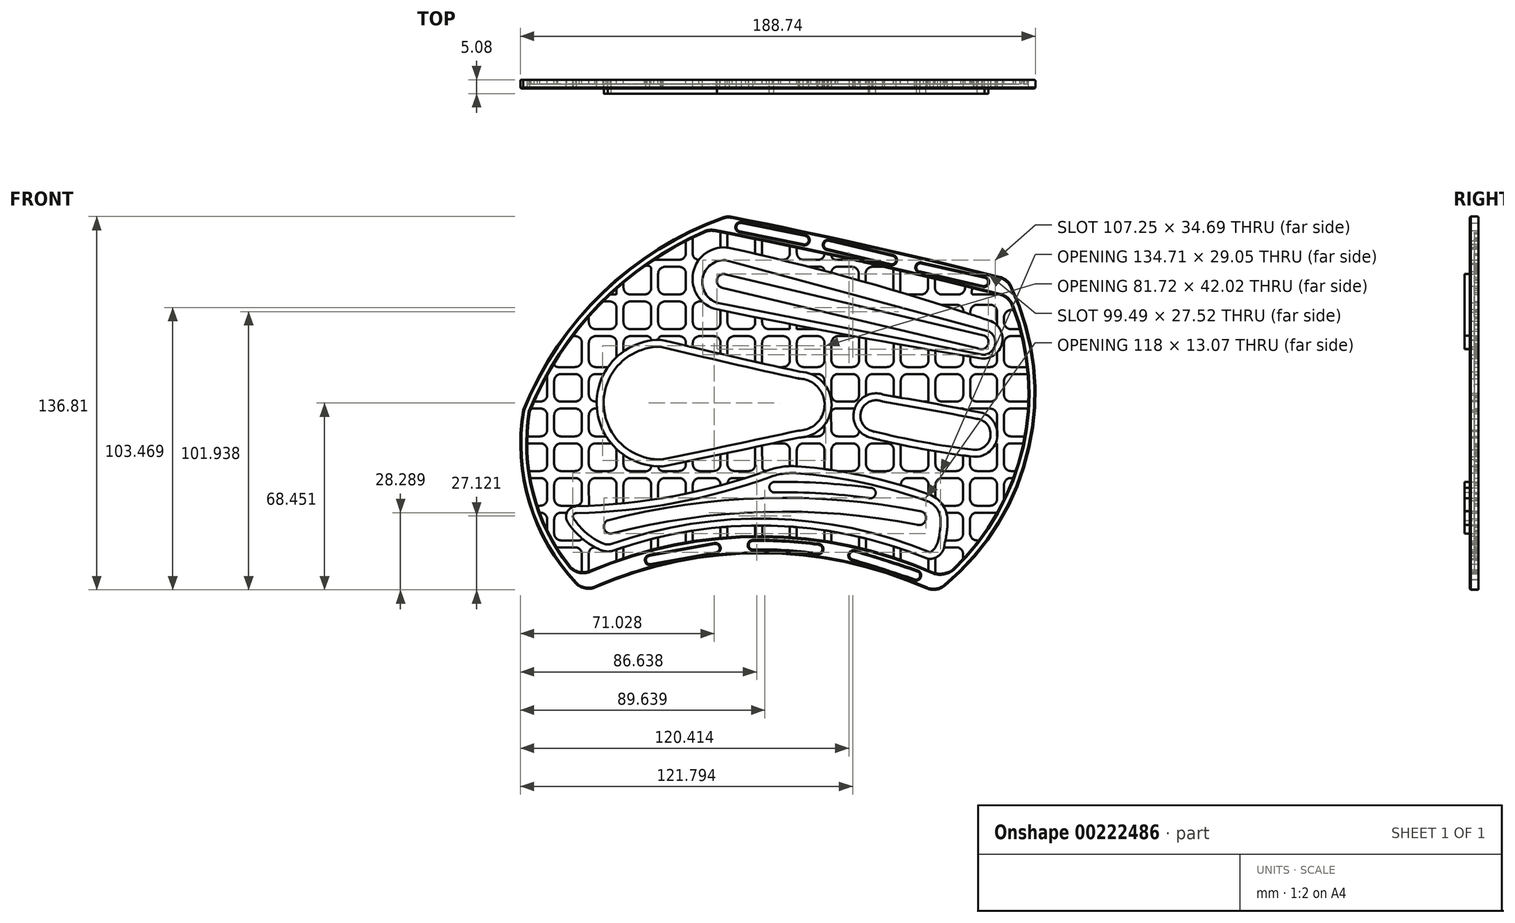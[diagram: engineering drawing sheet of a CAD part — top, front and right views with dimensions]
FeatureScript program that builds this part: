
annotation { "Feature Type Name" : "Feature", "Feature Type Description" : "" }
export const myFeature = defineFeature(function(context is Context, id is Id, definition is map)
    precondition{}
    {
        {
            var Q0;
            Q0=qCreatedBy(makeId("Front.planeOp"),FACE);
            var sketch = newSketch(context, id + "F7", { "sketchPlane" : qUnion([Q0])});
            skPoint(sketch, "E0.middle", {"position": v(0, 0) * mm});
            skPoint(sketch, "E1", {"position": v(94.45, -6.35) * mm});
            skPoint(sketch, "E2", {"position": v(-19.9, 68.07) * mm});
            skPoint(sketch, "E3", {"position": v(-72.19, -69.82) * mm});
            skPoint(sketch, "E4", {"position": v(56.54, -70) * mm});
            skPoint(sketch, "E5", {"position": v(-11.98, -55.6) * mm});
            skPoint(sketch, "E6.0.start.orphan", {"position": v(-11.98, -69.87) * mm});
            skArc(sketch, "E7", {"start": v(53.09, -68.42) * mm, "mid": v(-7.56, -55.54) * mm, "end": v(-68.28, -68.05) * mm});
            skArc(sketch, "E8", {"start": v(80.02, 45.68) * mm, "mid": v(31.06, 57.38) * mm, "end": v(-18.2, 67.74) * mm});
            skArc(sketch, "E9", {"start": v(-21.58, 67.48) * mm, "mid": v(-65.66, 40.06) * mm, "end": v(-94.71, -2.95) * mm});
            skArc(sketch, "E10", {"start": v(-94.71, -2.95) * mm, "mid": v(-92.54, -37.03) * mm, "end": v(-75.43, -66.58) * mm});
            skArc(sketch, "E11", {"start": v(59.69, -67.5) * mm, "mid": v(90.79, -16.84) * mm, "end": v(84.2, 42.24) * mm});
            skArc(sketch, "E12.filletArc", {"start": v(-75.43, -66.58) * mm, "mid": v(-72.08, -68.45) * mm, "end": v(-68.28, -68.05) * mm});
            skArc(sketch, "E13.filletArc", {"start": v(-18.2, 67.74) * mm, "mid": v(-19.9, 67.84) * mm, "end": v(-21.58, 67.48) * mm});
            skPoint(sketch, "E14.visualSharp", {"position": v(82.86, 44.96) * mm});
            skArc(sketch, "E14.filletArc", {"start": v(84.2, 42.24) * mm, "mid": v(82.5, 44.43) * mm, "end": v(80.02, 45.68) * mm});
            skArc(sketch, "E15.filletArc", {"start": v(53.09, -68.42) * mm, "mid": v(56.52, -68.9) * mm, "end": v(59.69, -67.5) * mm});
            skPoint(sketch, "E16.orphan", {"position": v(94.45, 69.85) * mm});
            skPoint(sketch, "E17.orphan", {"position": v(94.45, -69.85) * mm});
            skPoint(sketch, "E0.bottom.end.orphan", {"position": v(-94.45, -69.85) * mm});
            skPoint(sketch, "E0.right.end.orphan", {"position": v(-94.45, 69.85) * mm});
            skArc(sketch, "E18", {"start": v(73.3, 15.83) * mm, "mid": v(80.75, 21.2) * mm, "end": v(76.77, 29.48) * mm});
            skArc(sketch, "E19", {"start": v(-19.12, 56.36) * mm, "mid": v(-32.4, 47.29) * mm, "end": v(-23.6, 33.82) * mm});
            skArc(sketch, "E20", {"start": v(76.77, 29.48) * mm, "mid": v(29.2, 44.24) * mm, "end": v(-19.12, 56.36) * mm});
            skArc(sketch, "E21", {"start": v(-23.6, 33.82) * mm, "mid": v(24.76, 24.32) * mm, "end": v(73.3, 15.83) * mm});
            skArc(sketch, "E22.0", {"start": v(53.4, -57.51) * mm, "mid": v(-3.83, -45.43) * mm, "end": v(-61.62, -54.53) * mm});
            skArc(sketch, "E23", {"start": v(53.4, -57.51) * mm, "mid": v(57.85, -56.25) * mm, "end": v(59.69, -52) * mm});
            skArc(sketch, "E24.0", {"start": v(54.05, -33.95) * mm, "mid": v(30.26, -27.19) * mm, "end": v(5.78, -23.67) * mm});
            skPoint(sketch, "E25.end.orphan", {"position": v(53.09, -41.24) * mm});
            skArc(sketch, "E26", {"start": v(59.69, -52) * mm, "mid": v(60.56, -47.66) * mm, "end": v(60.77, -43.24) * mm});
            skArc(sketch, "E27", {"start": v(-78.33, -44.22) * mm, "mid": v(-73.03, -50.18) * mm, "end": v(-66.24, -54.37) * mm});
            skArc(sketch, "E28", {"start": v(-75.24, -38.32) * mm, "mid": v(-39.47, -34.58) * mm, "end": v(-4.77, -25.12) * mm});
            skPoint(sketch, "E29.visualSharp", {"position": v(0, -23.33) * mm});
            skArc(sketch, "E29.filletArc", {"start": v(5.78, -23.67) * mm, "mid": v(0.43, -23.84) * mm, "end": v(-4.77, -25.12) * mm});
            skPoint(sketch, "E30.visualSharp", {"position": v(-63.76, -55.3) * mm});
            skArc(sketch, "E30.filletArc", {"start": v(-66.24, -54.37) * mm, "mid": v(-63.95, -54.89) * mm, "end": v(-61.62, -54.53) * mm});
            skPoint(sketch, "E31.visualSharp", {"position": v(-81.25, -38.38) * mm});
            skArc(sketch, "E31.filletArc", {"start": v(-75.24, -38.32) * mm, "mid": v(-78.52, -40.36) * mm, "end": v(-78.33, -44.22) * mm});
            skPoint(sketch, "E32.visualSharp", {"position": v(59.69, -36.08) * mm});
            skArc(sketch, "E32.filletArc", {"start": v(60.77, -43.24) * mm, "mid": v(58.85, -37.56) * mm, "end": v(54.05, -33.95) * mm});
            skArc(sketch, "E33", {"start": v(-44.4, 20.12) * mm, "mid": v(-65.2, -0.8) * mm, "end": v(-43.84, -21.14) * mm});
            skArc(sketch, "E34", {"start": v(6.14, -10.59) * mm, "mid": v(15.76, -1.15) * mm, "end": v(6.3, 8.46) * mm});
            skArc(sketch, "E35", {"start": v(-44.4, 20.12) * mm, "mid": v(-19.07, 14.17) * mm, "end": v(6.3, 8.46) * mm});
            skArc(sketch, "E36", {"start": v(-43.84, -21.14) * mm, "mid": v(-18.83, -15.97) * mm, "end": v(6.14, -10.59) * mm});
            skPoint(sketch, "E37.orphan", {"position": v(-94.71, 103.33) * mm});
            skPoint(sketch, "E38.start.orphan", {"position": v(-72.08, -68.45) * mm});
            skArc(sketch, "E39", {"start": v(-20.7, 51.85) * mm, "mid": v(-28.93, 45.34) * mm, "end": v(-23.7, 36.24) * mm});
            skArc(sketch, "E40", {"start": v(73.76, 17.17) * mm, "mid": v(78.2, 20.73) * mm, "end": v(75.72, 25.85) * mm});
            skLineSegment(sketch, "E41", {"start": v(-20.7, 51.85) * mm, "end": v(75.72, 25.85) * mm});
            skLineSegment(sketch, "E42", {"start": v(73.76, 17.17) * mm, "end": v(-23.7, 36.24) * mm});
            skLineSegment(sketch, "E43.0", {"start": v(-21.78, 41.76) * mm, "end": v(71.73, 19.6) * mm});
            skLineSegment(sketch, "E44.0", {"start": v(-20.6, 46.7) * mm, "end": v(74.34, 24.2) * mm});
            skArc(sketch, "E45.0", {"start": v(-43.8, 22.6) * mm, "mid": v(-18.62, 16.67) * mm, "end": v(6.61, 11) * mm});
            skArc(sketch, "E46.0", {"start": v(-44.36, 22.66) * mm, "mid": v(-67.74, -0.82) * mm, "end": v(-43.75, -23.68) * mm});
            skArc(sketch, "E47.0", {"start": v(-43.34, -23.63) * mm, "mid": v(-18.44, -18.48) * mm, "end": v(6.42, -13.13) * mm});
            skArc(sketch, "E48.0", {"start": v(6.42, -13.13) * mm, "mid": v(18.3, -1.16) * mm, "end": v(6.61, 11) * mm});
            skLineSegment(sketch, "E49", {"start": v(-44.36, 22.66) * mm, "end": v(-43.8, 22.6) * mm});
            skLineSegment(sketch, "E50", {"start": v(-43.34, -23.63) * mm, "end": v(-43.75, -23.68) * mm});
            skArc(sketch, "E51.0", {"start": v(55.7, -62.63) * mm, "mid": v(24.98, -52.68) * mm, "end": v(-7.12, -49.2) * mm});
            skArc(sketch, "E52.0", {"start": v(80.08, 39.11) * mm, "mid": v(27.96, 51.57) * mm, "end": v(-24.51, 62.5) * mm});
            skArc(sketch, "E53.0", {"start": v(-28.27, 62.08) * mm, "mid": v(-66.68, 35.46) * mm, "end": v(-92.25, -3.65) * mm});
            skArc(sketch, "E54.0", {"start": v(-92.25, -3.65) * mm, "mid": v(-90.93, -33.4) * mm, "end": v(-77.7, -60.07) * mm});
            skArc(sketch, "E55.0", {"start": v(62.64, -61.51) * mm, "mid": v(88.27, -16.45) * mm, "end": v(84.44, 35.25) * mm});
            skPoint(sketch, "E56.visualSharp", {"position": v(83.19, 38.32) * mm});
            skArc(sketch, "E56.filletArc", {"start": v(84.44, 35.25) * mm, "mid": v(82.73, 37.71) * mm, "end": v(80.08, 39.11) * mm});
            skPoint(sketch, "E57.visualSharp", {"position": v(59.48, -64.36) * mm});
            skPoint(sketch, "E58.visualSharp", {"position": v(-74.47, -63.88) * mm});
            skArc(sketch, "E58.filletArc", {"start": v(-77.7, -60.07) * mm, "mid": v(-74.27, -62.3) * mm, "end": v(-70.2, -61.97) * mm});
            skPoint(sketch, "E59.visualSharp", {"position": v(-26.43, 62.86) * mm});
            skArc(sketch, "E59.filletArc", {"start": v(-24.51, 62.5) * mm, "mid": v(-26.42, 62.57) * mm, "end": v(-28.27, 62.08) * mm});
            skArc(sketch, "E60", {"start": v(37.02, 0) * mm, "mid": v(29.15, -3.47) * mm, "end": v(33.6, -10.83) * mm});
            skArc(sketch, "E61", {"start": v(70.58, -17.65) * mm, "mid": v(76.56, -12.36) * mm, "end": v(71.43, -6.25) * mm});
            skArc(sketch, "E62", {"start": v(71.43, -6.25) * mm, "mid": v(54.25, -2.98) * mm, "end": v(37.02, 0) * mm});
            skArc(sketch, "E63", {"start": v(33.6, -10.83) * mm, "mid": v(51.98, -14.83) * mm, "end": v(70.58, -17.65) * mm});
            skArc(sketch, "E64.0", {"start": v(33.06, -13.31) * mm, "mid": v(51.56, -17.33) * mm, "end": v(70.28, -20.17) * mm});
            skArc(sketch, "E65.0", {"start": v(71.82, -3.74) * mm, "mid": v(54.8, -0.5) * mm, "end": v(37.75, 2.46) * mm});
            skArc(sketch, "E66.0", {"start": v(37.75, 2.46) * mm, "mid": v(26.68, -2.84) * mm, "end": v(33.06, -13.31) * mm});
            skArc(sketch, "E67.0", {"start": v(70.46, -20.18) * mm, "mid": v(79.09, -12.62) * mm, "end": v(71.82, -3.74) * mm});
            skLineSegment(sketch, "E68", {"start": v(70.28, -20.17) * mm, "end": v(70.46, -20.18) * mm});
            skArc(sketch, "E69.0", {"start": v(53, -36.28) * mm, "mid": v(29.6, -29.64) * mm, "end": v(5.5, -26.2) * mm});
            skArc(sketch, "E70.0", {"start": v(54.44, -55.2) * mm, "mid": v(-3.73, -42.9) * mm, "end": v(-62.46, -52.14) * mm});
            skArc(sketch, "E71.0", {"start": v(57.17, -51.58) * mm, "mid": v(58.03, -47.4) * mm, "end": v(58.23, -43.13) * mm});
            skArc(sketch, "E72.0", {"start": v(-75.14, -40.86) * mm, "mid": v(-38.96, -37.06) * mm, "end": v(-3.86, -27.5) * mm});
            skArc(sketch, "E73.0", {"start": v(-76.2, -42.83) * mm, "mid": v(-71.4, -48.24) * mm, "end": v(-65.24, -52.04) * mm});
            skArc(sketch, "E74.0", {"start": v(5.58, -26.2) * mm, "mid": v(0.77, -26.35) * mm, "end": v(-3.9, -27.5) * mm});
            skArc(sketch, "E75", {"start": v(58.23, -43.13) * mm, "mid": v(56.71, -38.87) * mm, "end": v(53, -36.28) * mm});
            skArc(sketch, "E76", {"start": v(54.44, -55.2) * mm, "mid": v(56.15, -53.65) * mm, "end": v(57.17, -51.58) * mm});
            skArc(sketch, "E77", {"start": v(-75.14, -40.86) * mm, "mid": v(-76.33, -41.5) * mm, "end": v(-76.2, -42.83) * mm});
            skArc(sketch, "E78", {"start": v(-65.24, -52.04) * mm, "mid": v(-63.86, -52.32) * mm, "end": v(-62.46, -52.14) * mm});
            skArc(sketch, "E79", {"start": v(50.62, -40.1) * mm, "mid": v(-6.74, -35.32) * mm, "end": v(-63.7, -43.46) * mm});
            skArc(sketch, "E80.0", {"start": v(49.47, -45.04) * mm, "mid": v(-6.66, -40.4) * mm, "end": v(-62.43, -48.37) * mm});
            skArc(sketch, "E81", {"start": v(-63.7, -43.46) * mm, "mid": v(-65.04, -46.43) * mm, "end": v(-62.43, -48.37) * mm});
            skArc(sketch, "E82", {"start": v(31.81, -35.3) * mm, "mid": v(14.54, -33.61) * mm, "end": v(-2.81, -33.24) * mm});
            skArc(sketch, "E83.0", {"start": v(32.32, -31.52) * mm, "mid": v(14.77, -29.8) * mm, "end": v(-2.87, -29.43) * mm});
            skArc(sketch, "E84", {"start": v(-2.87, -29.43) * mm, "mid": v(-4.48, -31.36) * mm, "end": v(-2.81, -33.24) * mm});
            skArc(sketch, "E85", {"start": v(31.81, -35.3) * mm, "mid": v(34.46, -33.73) * mm, "end": v(32.32, -31.52) * mm});
            skArc(sketch, "E86", {"start": v(-20.6, 46.7) * mm, "mid": v(-23.67, 44.82) * mm, "end": v(-21.78, 41.76) * mm});
            skArc(sketch, "E87", {"start": v(71.73, 19.6) * mm, "mid": v(75.46, 20.53) * mm, "end": v(74.34, 24.2) * mm});
            skPoint(sketch, "E88.orphan", {"position": v(73.17, 24.48) * mm});
            skPoint(sketch, "E89.end.orphan", {"position": v(73.17, 19.26) * mm});
            skLineSegment(sketch, "E90.0", {"start": v(-80.78, -50.81) * mm, "end": v(-74, -50.81) * mm});
            skLineSegment(sketch, "E91.0", {"start": v(-89.53, -38.11) * mm, "end": v(-88.4, -38.11) * mm});
            skLineSegment(sketch, "E92.0", {"start": v(-92.51, -25.41) * mm, "end": v(-88.4, -25.41) * mm});
            skLineSegment(sketch, "E93.0", {"start": v(-93.16, -12.71) * mm, "end": v(-88.4, -12.71) * mm});
            skLineSegment(sketch, "E94.0", {"start": v(-62.8, 39.28) * mm, "end": v(-60.46, 39.28) * mm});
            skLineSegment(sketch, "E95.0", {"start": v(-46.77, 51.98) * mm, "end": v(-37.6, 51.98) * mm});
            skLineSegment(sketch, "E96.trimOffspring", {"start": v(-0.33, 51.98) * mm, "end": v(0.5, 51.98) * mm});
            skLineSegment(sketch, "E97.trimOffspring", {"start": v(46.24, 39.28) * mm, "end": v(51.1, 39.28) * mm});
            skLineSegment(sketch, "E98.trimOffspring", {"start": v(84.04, 26.58) * mm, "end": v(87.3, 26.58) * mm});
            skLineSegment(sketch, "E99.trimOffspring", {"start": v(52.03, 0) * mm, "end": v(53.84, 0) * mm});
            skLineSegment(sketch, "E100.trimOffspring", {"start": v(78.96, -12.71) * mm, "end": v(79.08, -12.71) * mm});
            skLineSegment(sketch, "E101.trimOffspring", {"start": v(20.78, 0) * mm, "end": v(25.9, 0) * mm});
            skLineSegment(sketch, "E102.trimOffspring", {"start": v(-82.04, 12.69) * mm, "end": v(-75.7, 12.69) * mm});
            skLineSegment(sketch, "E103.trimOffspring", {"start": v(-1.03, 12.69) * mm, "end": v(0.5, 12.69) * mm});
            skLineSegment(sketch, "E104.trimOffspring", {"start": v(9.38, -12.71) * mm, "end": v(13.16, -12.71) * mm});
            skLineSegment(sketch, "E105.trimOffspring", {"start": v(-90.68, 0.05) * mm, "end": v(-88.4, 0.05) * mm});
            skLineSegment(sketch, "E106.trimOffspring", {"start": v(60, -50.81) * mm, "end": v(63.95, -50.81) * mm});
            skLineSegment(sketch, "E107.trimOffspring", {"start": v(59.22, -38.11) * mm, "end": v(63.95, -38.11) * mm});
            skLineSegment(sketch, "E108.trimOffspring", {"start": v(20.69, -25.41) * mm, "end": v(25.9, -25.41) * mm});
            skArc(sketch, "E109", {"start": v(49.47, -45.04) * mm, "mid": v(52.87, -43.22) * mm, "end": v(50.62, -40.1) * mm});
            skArc(sketch, "E110", {"start": v(55.7, -62.63) * mm, "mid": v(59.31, -62.94) * mm, "end": v(62.64, -61.51) * mm});
            skLineSegment(sketch, "E111.0", {"start": v(56.19, 45.02) * mm, "end": v(56.19, 41.82) * mm});
            skLineSegment(sketch, "E112.0", {"start": v(43.49, 48.02) * mm, "end": v(43.49, 40.1) * mm});
            skLineSegment(sketch, "E113.0", {"start": v(30.79, 46.9) * mm, "end": v(30.79, 43.8) * mm});
            skLineSegment(sketch, "E114.0", {"start": v(-32.52, 60.11) * mm, "end": v(-32.52, 53.86) * mm});
            skLineSegment(sketch, "E115.0", {"start": v(-45.22, 46.9) * mm, "end": v(-45.22, 41.82) * mm});
            skLineSegment(sketch, "E116.0", {"start": v(-57.92, 43.62) * mm, "end": v(-57.92, 41.82) * mm});
            skLineSegment(sketch, "E117.0", {"start": v(-70.62, 31.21) * mm, "end": v(-70.62, 29.12) * mm});
            skLineSegment(sketch, "E118.trimOffspring", {"start": v(69.03, -20.02) * mm, "end": v(69.03, -22.87) * mm});
            skLineSegment(sketch, "E119.trimOffspring", {"start": v(69.1, 16.53) * mm, "end": v(69.1, 15.23) * mm});
            skLineSegment(sketch, "E120.trimOffspring", {"start": v(69.8, 41.7) * mm, "end": v(69.67, 39.82) * mm});
            skLineSegment(sketch, "E121.trimOffspring", {"start": v(43.67, 20.89) * mm, "end": v(43.67, 15.23) * mm});
            skLineSegment(sketch, "E122.trimOffspring", {"start": v(30.97, 23.18) * mm, "end": v(30.97, 15.23) * mm});
            skLineSegment(sketch, "E123.trimOffspring", {"start": v(56.38, 18.67) * mm, "end": v(56.38, 15.23) * mm});
            skLineSegment(sketch, "E124.trimOffspring", {"start": v(18.24, 21.5) * mm, "end": v(18.24, 15.23) * mm});
            skLineSegment(sketch, "E125.trimOffspring", {"start": v(5.58, 56.42) * mm, "end": v(5.58, 54.52) * mm});
            skLineSegment(sketch, "E126.trimOffspring", {"start": v(-7.12, 59.05) * mm, "end": v(-7.12, 53.61) * mm});
            skLineSegment(sketch, "E127.trimOffspring", {"start": v(-19.83, 61.58) * mm, "end": v(-19.83, 56.46) * mm});
            skLineSegment(sketch, "E128.trimOffspring", {"start": v(-70.62, -55.7) * mm, "end": v(-70.62, -62.13) * mm});
            skLineSegment(sketch, "E129.trimOffspring", {"start": v(-57.92, -53.28) * mm, "end": v(-57.92, -57.3) * mm});
            skLineSegment(sketch, "E130.trimOffspring", {"start": v(-45.22, -49.72) * mm, "end": v(-45.22, -53.64) * mm});
            skLineSegment(sketch, "E131.trimOffspring", {"start": v(-32.52, -47.25) * mm, "end": v(-32.52, -51.1) * mm});
            skLineSegment(sketch, "E132.trimOffspring", {"start": v(-19.83, -45.81) * mm, "end": v(-19.83, -49.63) * mm});
            skLineSegment(sketch, "E133.trimOffspring", {"start": v(43.67, -53.87) * mm, "end": v(43.67, -57.9) * mm});
            skLineSegment(sketch, "E134.trimOffspring", {"start": v(56.38, -57.16) * mm, "end": v(56.38, -62.83) * mm});
            skLineSegment(sketch, "E135.trimOffspring", {"start": v(30.97, -50.16) * mm, "end": v(30.97, -54.09) * mm});
            skLineSegment(sketch, "E136.trimOffspring", {"start": v(18.24, -47.53) * mm, "end": v(18.24, -51.4) * mm});
            skLineSegment(sketch, "E137.trimOffspring", {"start": v(5.58, -17.8) * mm, "end": v(5.58, -23.66) * mm});
            skLineSegment(sketch, "E138.trimOffspring", {"start": v(-7.12, -16.07) * mm, "end": v(-7.12, -24.06) * mm});
            skLineSegment(sketch, "E139.trimOffspring", {"start": v(-19.83, -18.78) * mm, "end": v(-19.83, -22.87) * mm});
            skLineSegment(sketch, "E140.trimOffspring", {"start": v(-32.52, -21.42) * mm, "end": v(-32.52, -22.87) * mm});
            skLineSegment(sketch, "E141.trimOffspring", {"start": v(-57.92, -19.46) * mm, "end": v(-57.92, -22.87) * mm});
            skLineSegment(sketch, "E142.trimOffspring", {"start": v(30.97, -12.62) * mm, "end": v(30.97, -12.71) * mm});
            skLineSegment(sketch, "E143.trimOffspring", {"start": v(43.67, -15.77) * mm, "end": v(43.67, -22.87) * mm});
            skLineSegment(sketch, "E144.trimOffspring", {"start": v(56.38, -18.18) * mm, "end": v(56.38, -22.87) * mm});
            skLineSegment(sketch, "E145.0", {"start": v(78.97, 39.4) * mm, "end": v(78.97, 39.28) * mm});
            skLineSegment(sketch, "E146.0", {"start": v(67.3, 42.32) * mm, "end": v(67.25, 41.64) * mm});
            skLineSegment(sketch, "E147.0", {"start": v(53.65, 45.63) * mm, "end": v(53.65, 41.82) * mm});
            skLineSegment(sketch, "E148.trimOffspring", {"start": v(84.04, 33.53) * mm, "end": v(85.09, 33.53) * mm});
            skLineSegment(sketch, "E149.trimOffspring", {"start": v(81.5, 31) * mm, "end": v(81.5, 29.12) * mm});
            skLineSegment(sketch, "E150.trimOffspring", {"start": v(78.96, 33) * mm, "end": v(78.96, 27.94) * mm});
            skLineSegment(sketch, "E151.0", {"start": v(84.04, 24.04) * mm, "end": v(87.95, 24.04) * mm});
            skLineSegment(sketch, "E152.trimOffspring", {"start": v(78.96, 18) * mm, "end": v(78.96, 15.23) * mm});
            skLineSegment(sketch, "E153.trimOffspring", {"start": v(81.5, 21.5) * mm, "end": v(81.5, 15.23) * mm});
            skLineSegment(sketch, "E154.0", {"start": v(10.7, 10.15) * mm, "end": v(13.16, 10.15) * mm});
            skLineSegment(sketch, "E155.trimOffspring", {"start": v(84.04, 12.69) * mm, "end": v(89.93, 12.69) * mm});
            skLineSegment(sketch, "E156.trimOffspring", {"start": v(81.5, 7.6) * mm, "end": v(81.5, 2.54) * mm});
            skLineSegment(sketch, "E157.trimOffspring", {"start": v(84.04, 10.15) * mm, "end": v(90.17, 10.15) * mm});
            skLineSegment(sketch, "E158.trimOffspring", {"start": v(78.96, 7.6) * mm, "end": v(78.96, 2.54) * mm});
            skLineSegment(sketch, "E159.0", {"start": v(65.7, -2.54) * mm, "end": v(66.56, -2.54) * mm});
            skLineSegment(sketch, "E160.trimOffspring", {"start": v(81.5, -5.08) * mm, "end": v(81.5, -10.17) * mm});
            skLineSegment(sketch, "E161.trimOffspring", {"start": v(84.04, 0) * mm, "end": v(90.4, 0) * mm});
            skLineSegment(sketch, "E162.trimOffspring", {"start": v(78.96, -5.08) * mm, "end": v(78.96, -12.71) * mm});
            skLineSegment(sketch, "E163.trimOffspring", {"start": v(84.04, -2.54) * mm, "end": v(90.27, -2.54) * mm});
            skLineSegment(sketch, "E164.0", {"start": v(78.42, -15.25) * mm, "end": v(78.96, -15.25) * mm});
            skLineSegment(sketch, "E165.trimOffspring", {"start": v(84.04, -12.71) * mm, "end": v(89.03, -12.71) * mm});
            skLineSegment(sketch, "E166.trimOffspring", {"start": v(78.96, -15.25) * mm, "end": v(78.96, -22.87) * mm});
            skLineSegment(sketch, "E167.trimOffspring", {"start": v(81.5, -17.8) * mm, "end": v(81.5, -22.87) * mm});
            skLineSegment(sketch, "E168.trimOffspring", {"start": v(84.04, -15.25) * mm, "end": v(88.53, -15.25) * mm});
            skLineSegment(sketch, "E169.trimOffspring", {"start": v(81.5, -30.5) * mm, "end": v(81.5, -35.8) * mm});
            skLineSegment(sketch, "E170.trimOffspring", {"start": v(84.04, -25.41) * mm, "end": v(85.75, -25.41) * mm});
            skLineSegment(sketch, "E171.trimOffspring", {"start": v(84.04, -27.95) * mm, "end": v(84.85, -27.95) * mm});
            skLineSegment(sketch, "E172.trimOffspring", {"start": v(78.96, -30.5) * mm, "end": v(78.96, -35.57) * mm});
            skLineSegment(sketch, "E173.0", {"start": v(66.56, 16.95) * mm, "end": v(66.56, 15.23) * mm});
            skLineSegment(sketch, "E174.0", {"start": v(53.84, 19.11) * mm, "end": v(53.84, 15.23) * mm});
            skLineSegment(sketch, "E175.trimOffspring", {"start": v(69.1, 7.6) * mm, "end": v(69.1, 2.54) * mm});
            skLineSegment(sketch, "E176.trimOffspring", {"start": v(71.64, 12.69) * mm, "end": v(76.42, 12.69) * mm});
            skLineSegment(sketch, "E177.trimOffspring", {"start": v(71.64, 10.15) * mm, "end": v(76.42, 10.15) * mm});
            skLineSegment(sketch, "E178.trimOffspring", {"start": v(66.56, 7.6) * mm, "end": v(66.56, 2.54) * mm});
            skLineSegment(sketch, "E179.trimOffspring", {"start": v(58.92, 0) * mm, "end": v(64.02, 0) * mm});
            skLineSegment(sketch, "E180.trimOffspring", {"start": v(71.64, 0) * mm, "end": v(76.42, 0) * mm});
            skLineSegment(sketch, "E181.trimOffspring", {"start": v(69.1, -2.54) * mm, "end": v(69.1, -3.2) * mm});
            skLineSegment(sketch, "E182.trimOffspring", {"start": v(69.1, -2.54) * mm, "end": v(76.42, -2.54) * mm});
            skLineSegment(sketch, "E183.trimOffspring", {"start": v(66.56, -2.54) * mm, "end": v(66.56, -2.7) * mm});
            skLineSegment(sketch, "E184.trimOffspring", {"start": v(58.92, 12.69) * mm, "end": v(64.02, 12.69) * mm});
            skLineSegment(sketch, "E185.trimOffspring", {"start": v(56.38, 7.6) * mm, "end": v(56.38, 2.54) * mm});
            skLineSegment(sketch, "E186.trimOffspring", {"start": v(58.92, 10.15) * mm, "end": v(64.02, 10.15) * mm});
            skLineSegment(sketch, "E187.trimOffspring", {"start": v(53.84, 7.6) * mm, "end": v(53.84, 0) * mm});
            skLineSegment(sketch, "E188.0", {"start": v(41.13, 21.34) * mm, "end": v(41.13, 15.23) * mm});
            skLineSegment(sketch, "E189.trimOffspring", {"start": v(46.21, 12.69) * mm, "end": v(51.3, 12.69) * mm});
            skLineSegment(sketch, "E190.trimOffspring", {"start": v(43.67, 7.6) * mm, "end": v(43.67, 1.46) * mm});
            skLineSegment(sketch, "E191.trimOffspring", {"start": v(46.21, 10.15) * mm, "end": v(51.3, 10.15) * mm});
            skLineSegment(sketch, "E192.trimOffspring", {"start": v(41.13, 7.6) * mm, "end": v(41.13, 1.9) * mm});
            skLineSegment(sketch, "E193.trimOffspring", {"start": v(58.73, 39.28) * mm, "end": v(64.72, 39.28) * mm});
            skLineSegment(sketch, "E194.trimOffspring", {"start": v(58.35, 35.54) * mm, "end": v(64.1, 35.54) * mm});
            skLineSegment(sketch, "E195.0", {"start": v(40.95, 48.61) * mm, "end": v(40.95, 40.86) * mm});
            skLineSegment(sketch, "E196.0", {"start": v(-85.86, 9.7) * mm, "end": v(-85.86, 2.59) * mm});
            skLineSegment(sketch, "E197.0", {"start": v(-91.78, -2.5) * mm, "end": v(-88.4, -2.5) * mm});
            skLineSegment(sketch, "E198.0", {"start": v(-93.21, -15.25) * mm, "end": v(-88.4, -15.25) * mm});
            skLineSegment(sketch, "E199.0", {"start": v(-92.1, -27.95) * mm, "end": v(-88.4, -27.95) * mm});
            skLineSegment(sketch, "E200.trimOffspring", {"start": v(-80.78, 0.05) * mm, "end": v(-75.7, 0.05) * mm});
            skLineSegment(sketch, "E201.trimOffspring", {"start": v(-83.32, -5.03) * mm, "end": v(-83.32, -10.17) * mm});
            skLineSegment(sketch, "E202.trimOffspring", {"start": v(-80.78, -2.5) * mm, "end": v(-75.7, -2.5) * mm});
            skLineSegment(sketch, "E203.trimOffspring", {"start": v(-85.86, -5.03) * mm, "end": v(-85.86, -10.17) * mm});
            skLineSegment(sketch, "E204.trimOffspring", {"start": v(-80.78, -12.71) * mm, "end": v(-75.7, -12.71) * mm});
            skLineSegment(sketch, "E205.trimOffspring", {"start": v(-80.78, -15.25) * mm, "end": v(-75.7, -15.25) * mm});
            skLineSegment(sketch, "E206.trimOffspring", {"start": v(-83.32, -17.8) * mm, "end": v(-83.32, -22.87) * mm});
            skLineSegment(sketch, "E207.trimOffspring", {"start": v(-85.86, -17.8) * mm, "end": v(-85.86, -22.87) * mm});
            skLineSegment(sketch, "E208.trimOffspring", {"start": v(-80.78, -27.95) * mm, "end": v(-75.7, -27.95) * mm});
            skLineSegment(sketch, "E209.trimOffspring", {"start": v(-80.78, -25.41) * mm, "end": v(-75.7, -25.41) * mm});
            skLineSegment(sketch, "E210.trimOffspring", {"start": v(-83.32, -30.5) * mm, "end": v(-83.32, -35.57) * mm});
            skLineSegment(sketch, "E211.trimOffspring", {"start": v(-85.86, -30.5) * mm, "end": v(-85.86, -35.57) * mm});
            skLineSegment(sketch, "E212.trimOffspring", {"start": v(-68.08, -25.41) * mm, "end": v(-63, -25.41) * mm});
            skLineSegment(sketch, "E213.trimOffspring", {"start": v(-73.16, -30.5) * mm, "end": v(-73.16, -36.22) * mm});
            skLineSegment(sketch, "E214.trimOffspring", {"start": v(-68.08, -12.71) * mm, "end": v(-64.28, -12.71) * mm});
            skLineSegment(sketch, "E215.trimOffspring", {"start": v(-68.08, -15.25) * mm, "end": v(-62.46, -15.25) * mm});
            skLineSegment(sketch, "E216.trimOffspring", {"start": v(-70.62, -17.8) * mm, "end": v(-70.62, -22.87) * mm});
            skLineSegment(sketch, "E217.trimOffspring", {"start": v(-73.16, -17.8) * mm, "end": v(-73.16, -22.87) * mm});
            skLineSegment(sketch, "E218.trimOffspring", {"start": v(-68.08, 0.05) * mm, "end": v(-67.74, 0.05) * mm});
            skLineSegment(sketch, "E219.trimOffspring", {"start": v(-68.08, -2.5) * mm, "end": v(-67.66, -2.5) * mm});
            skLineSegment(sketch, "E220.trimOffspring", {"start": v(-70.62, -5.03) * mm, "end": v(-70.62, -10.17) * mm});
            skLineSegment(sketch, "E221.trimOffspring", {"start": v(-73.16, -5.03) * mm, "end": v(-73.16, -10.17) * mm});
            skLineSegment(sketch, "E222.0", {"start": v(28.43, 23.64) * mm, "end": v(28.43, 15.23) * mm});
            skLineSegment(sketch, "E223.trimOffspring", {"start": v(30.97, 7.6) * mm, "end": v(30.97, 2.23) * mm});
            skLineSegment(sketch, "E224.trimOffspring", {"start": v(28.43, 7.6) * mm, "end": v(28.43, 2.54) * mm});
            skLineSegment(sketch, "E225.trimOffspring", {"start": v(33.51, 12.69) * mm, "end": v(38.6, 12.69) * mm});
            skLineSegment(sketch, "E226.trimOffspring", {"start": v(33.51, 10.15) * mm, "end": v(38.6, 10.15) * mm});
            skLineSegment(sketch, "E227.0", {"start": v(53.84, -17.74) * mm, "end": v(53.84, -22.87) * mm});
            skLineSegment(sketch, "E228.trimOffspring", {"start": v(58.92, -27.95) * mm, "end": v(63.95, -27.95) * mm});
            skLineSegment(sketch, "E229.trimOffspring", {"start": v(58.92, -25.41) * mm, "end": v(63.95, -25.41) * mm});
            skLineSegment(sketch, "E230.trimOffspring", {"start": v(56.38, -30.5) * mm, "end": v(56.38, -35.15) * mm});
            skLineSegment(sketch, "E231.trimOffspring", {"start": v(53.84, -30.5) * mm, "end": v(53.84, -33.88) * mm});
            skLineSegment(sketch, "E232.0", {"start": v(66.5, -19.7) * mm, "end": v(66.5, -22.87) * mm});
            skLineSegment(sketch, "E233.0", {"start": v(60.36, -40.65) * mm, "end": v(63.95, -40.65) * mm});
            skLineSegment(sketch, "E234.trimOffspring", {"start": v(71.57, -25.41) * mm, "end": v(76.42, -25.41) * mm});
            skLineSegment(sketch, "E235.trimOffspring", {"start": v(69.03, -30.5) * mm, "end": v(69.03, -35.57) * mm});
            skLineSegment(sketch, "E236.trimOffspring", {"start": v(71.57, -27.95) * mm, "end": v(76.42, -27.95) * mm});
            skLineSegment(sketch, "E237.trimOffspring", {"start": v(66.5, -30.5) * mm, "end": v(66.5, -35.57) * mm});
            skLineSegment(sketch, "E238.trimOffspring", {"start": v(71.57, -38.11) * mm, "end": v(76.42, -38.11) * mm});
            skLineSegment(sketch, "E239.trimOffspring", {"start": v(66.5, -43.2) * mm, "end": v(66.5, -48.27) * mm});
            skLineSegment(sketch, "E240.trimOffspring", {"start": v(71.57, -40.65) * mm, "end": v(79.2, -40.65) * mm});
            skLineSegment(sketch, "E241.trimOffspring", {"start": v(69.03, -43.2) * mm, "end": v(69.03, -48.27) * mm});
            skLineSegment(sketch, "E242.0", {"start": v(41.13, -17.8) * mm, "end": v(41.13, -22.87) * mm});
            skLineSegment(sketch, "E243.trimOffspring", {"start": v(46.21, -25.41) * mm, "end": v(51.3, -25.41) * mm});
            skLineSegment(sketch, "E244.trimOffspring", {"start": v(46.21, -27.95) * mm, "end": v(51.3, -27.95) * mm});
            skLineSegment(sketch, "E245.trimOffspring", {"start": v(43.67, -30.5) * mm, "end": v(43.67, -30.8) * mm});
            skLineSegment(sketch, "E246.trimOffspring", {"start": v(33.51, -25.41) * mm, "end": v(38.6, -25.41) * mm});
            skLineSegment(sketch, "E247.trimOffspring", {"start": v(70.17, 39.28) * mm, "end": v(78.97, 39.28) * mm});
            skLineSegment(sketch, "E248.trimOffspring", {"start": v(71.73, 35.54) * mm, "end": v(76.42, 35.54) * mm});
            skLineSegment(sketch, "E249.trimOffspring", {"start": v(69.2, 33.18) * mm, "end": v(69.12, 32.05) * mm});
            skLineSegment(sketch, "E250.trimOffspring", {"start": v(66.63, 32.87) * mm, "end": v(66.63, 32.82) * mm});
            skLineSegment(sketch, "E251.0", {"start": v(59.56, -53.35) * mm, "end": v(63.95, -53.35) * mm});
            skLineSegment(sketch, "E252.trimOffspring", {"start": v(71.57, -50.81) * mm, "end": v(72.25, -50.81) * mm});
            skLineSegment(sketch, "E253.trimOffspring", {"start": v(66.5, -55.9) * mm, "end": v(66.5, -57.64) * mm});
            skLineSegment(sketch, "E254", {"start": v(30.97, -17.8) * mm, "end": v(30.97, -22.87) * mm});
            skLineSegment(sketch, "E255.0", {"start": v(28.25, 46.9) * mm, "end": v(28.25, 44.5) * mm});
            skLineSegment(sketch, "E256.0", {"start": v(9.82, 49.44) * mm, "end": v(14.26, 49.44) * mm});
            skLineSegment(sketch, "E257.trimOffspring", {"start": v(33.33, 49.44) * mm, "end": v(37.35, 49.44) * mm});
            skLineSegment(sketch, "E258.trimOffspring", {"start": v(20.42, 49.44) * mm, "end": v(25.7, 49.44) * mm});
            skLineSegment(sketch, "E259.trimOffspring", {"start": v(19.87, 51.98) * mm, "end": v(26.1, 51.98) * mm});
            skLineSegment(sketch, "E260.0", {"start": v(15.7, 21.5) * mm, "end": v(15.7, 15.23) * mm});
            skLineSegment(sketch, "E261.trimOffspring", {"start": v(20.78, 12.69) * mm, "end": v(25.9, 12.69) * mm});
            skLineSegment(sketch, "E262.trimOffspring", {"start": v(20.78, 10.15) * mm, "end": v(25.9, 10.15) * mm});
            skLineSegment(sketch, "E263.trimOffspring", {"start": v(18.24, 7.6) * mm, "end": v(18.24, 2.53) * mm});
            skLineSegment(sketch, "E264.trimOffspring", {"start": v(15.7, 7.6) * mm, "end": v(15.7, 6.42) * mm});
            skLineSegment(sketch, "E265.0", {"start": v(3.04, 56.96) * mm, "end": v(3.04, 54.52) * mm});
            skLineSegment(sketch, "E266.0", {"start": v(-76.5, 24.04) * mm, "end": v(-75.7, 24.04) * mm});
            skLineSegment(sketch, "E267.trimOffspring", {"start": v(5.58, 26.58) * mm, "end": v(12.75, 26.58) * mm});
            skLineSegment(sketch, "E268.trimOffspring", {"start": v(8.12, 24.04) * mm, "end": v(13.16, 24.04) * mm});
            skLineSegment(sketch, "E269.trimOffspring", {"start": v(5.58, 21.5) * mm, "end": v(5.58, 15.23) * mm});
            skLineSegment(sketch, "E270.trimOffspring", {"start": v(3.04, 21.5) * mm, "end": v(3.04, 15.23) * mm});
            skLineSegment(sketch, "E271.trimOffspring", {"start": v(20.78, 24.04) * mm, "end": v(26.27, 24.04) * mm});
            skLineSegment(sketch, "E272.0", {"start": v(-9.66, 59.56) * mm, "end": v(-9.66, 54.2) * mm});
            skLineSegment(sketch, "E273.trimOffspring", {"start": v(-4.58, 24.04) * mm, "end": v(0.5, 24.04) * mm});
            skLineSegment(sketch, "E274.trimOffspring", {"start": v(-4.58, 26.58) * mm, "end": v(3.04, 26.58) * mm});
            skLineSegment(sketch, "E275.trimOffspring", {"start": v(-7.12, 21.5) * mm, "end": v(-7.12, 14.05) * mm});
            skLineSegment(sketch, "E276.trimOffspring", {"start": v(-9.66, 21.5) * mm, "end": v(-9.66, 14.63) * mm});
            skLineSegment(sketch, "E277.trimOffspring", {"start": v(8.12, 12.69) * mm, "end": v(13.16, 12.69) * mm});
            skLineSegment(sketch, "E278.0", {"start": v(19.6, -2.55) * mm, "end": v(26.78, -2.54) * mm});
            skLineSegment(sketch, "E279.trimOffspring", {"start": v(15.7, -8.55) * mm, "end": v(15.7, -10.17) * mm});
            skLineSegment(sketch, "E280.0", {"start": v(-3.31, -15.25) * mm, "end": v(0.5, -15.25) * mm});
            skLineSegment(sketch, "E281.trimOffspring", {"start": v(30.97, -12.71) * mm, "end": v(31.17, -12.71) * mm});
            skLineSegment(sketch, "E282.trimOffspring", {"start": v(33.51, -15.25) * mm, "end": v(38.6, -15.25) * mm});
            skLineSegment(sketch, "E283.trimOffspring", {"start": v(28.43, -17.8) * mm, "end": v(28.43, -22.87) * mm});
            skLineSegment(sketch, "E284.trimOffspring", {"start": v(18.24, -17.8) * mm, "end": v(18.24, -25.04) * mm});
            skLineSegment(sketch, "E285.trimOffspring", {"start": v(20.73, -12.71) * mm, "end": v(26.7, -12.71) * mm});
            skLineSegment(sketch, "E286.trimOffspring", {"start": v(20.78, -15.25) * mm, "end": v(25.9, -15.25) * mm});
            skLineSegment(sketch, "E287.trimOffspring", {"start": v(15.7, -17.8) * mm, "end": v(15.7, -25.04) * mm});
            skLineSegment(sketch, "E288.0", {"start": v(3.04, -17.8) * mm, "end": v(3.04, -23.62) * mm});
            skLineSegment(sketch, "E289.trimOffspring", {"start": v(8.12, -15.25) * mm, "end": v(13.16, -15.25) * mm});
            skLineSegment(sketch, "E290.trimOffspring", {"start": v(5.58, -45.95) * mm, "end": v(5.58, -49.78) * mm});
            skLineSegment(sketch, "E291.trimOffspring", {"start": v(3.04, -45.76) * mm, "end": v(3.04, -49.78) * mm});
            skLineSegment(sketch, "E292.trimOffspring", {"start": v(-7.12, -45.38) * mm, "end": v(-7.12, -49.2) * mm});
            skLineSegment(sketch, "E293.0", {"start": v(-65.42, 36.74) * mm, "end": v(-63, 36.74) * mm});
            skLineSegment(sketch, "E294.0", {"start": v(-22.37, 62.08) * mm, "end": v(-22.37, 56.47) * mm});
            skLineSegment(sketch, "E295.0", {"start": v(-35.06, 58.84) * mm, "end": v(-35.06, 54.52) * mm});
            skLineSegment(sketch, "E296.0", {"start": v(-47.76, 48.9) * mm, "end": v(-47.76, 41.82) * mm});
            skLineSegment(sketch, "E297.0", {"start": v(-60.46, 41.41) * mm, "end": v(-60.46, 39.28) * mm});
            skLineSegment(sketch, "E298.trimOffspring", {"start": v(-17.29, 24.04) * mm, "end": v(-12.2, 24.04) * mm});
            skLineSegment(sketch, "E299.trimOffspring", {"start": v(-17.29, 26.58) * mm, "end": v(-12.2, 26.58) * mm});
            skLineSegment(sketch, "E300.trimOffspring", {"start": v(-22.37, 21.5) * mm, "end": v(-22.37, 17.54) * mm});
            skLineSegment(sketch, "E301.trimOffspring", {"start": v(-19.83, 21.5) * mm, "end": v(-19.83, 16.95) * mm});
            skLineSegment(sketch, "E302.trimOffspring", {"start": v(-29.98, 26.58) * mm, "end": v(-24.9, 26.58) * mm});
            skLineSegment(sketch, "E303.trimOffspring", {"start": v(-29.98, 24.04) * mm, "end": v(-24.9, 24.04) * mm});
            skLineSegment(sketch, "E304.trimOffspring", {"start": v(-35.06, 21.5) * mm, "end": v(-35.06, 20.5) * mm});
            skLineSegment(sketch, "E305.trimOffspring", {"start": v(-32.52, 21.5) * mm, "end": v(-32.52, 19.9) * mm});
            skLineSegment(sketch, "E306.trimOffspring", {"start": v(-32.52, 34.2) * mm, "end": v(-32.52, 29.12) * mm});
            skLineSegment(sketch, "E307.trimOffspring", {"start": v(-35.06, 34.2) * mm, "end": v(-35.06, 29.12) * mm});
            skLineSegment(sketch, "E308.trimOffspring", {"start": v(-29.98, 36.74) * mm, "end": v(-29.08, 36.74) * mm});
            skLineSegment(sketch, "E309.trimOffspring", {"start": v(-45.22, 34.2) * mm, "end": v(-45.22, 29.12) * mm});
            skLineSegment(sketch, "E310.trimOffspring", {"start": v(-42.68, 39.28) * mm, "end": v(-37.6, 39.28) * mm});
            skLineSegment(sketch, "E311.trimOffspring", {"start": v(-42.68, 36.74) * mm, "end": v(-37.6, 36.74) * mm});
            skLineSegment(sketch, "E312.trimOffspring", {"start": v(-42.68, 26.58) * mm, "end": v(-37.6, 26.58) * mm});
            skLineSegment(sketch, "E313.trimOffspring", {"start": v(-44, 24.04) * mm, "end": v(-37.6, 24.04) * mm});
            skLineSegment(sketch, "E314.trimOffspring", {"start": v(-47.76, 34.2) * mm, "end": v(-47.76, 29.12) * mm});
            skLineSegment(sketch, "E315.trimOffspring", {"start": v(-55.38, 39.28) * mm, "end": v(-50.3, 39.28) * mm});
            skLineSegment(sketch, "E316.trimOffspring", {"start": v(-57.92, 34.2) * mm, "end": v(-57.92, 29.12) * mm});
            skLineSegment(sketch, "E317.trimOffspring", {"start": v(-60.46, 34.2) * mm, "end": v(-60.46, 29.12) * mm});
            skLineSegment(sketch, "E318.trimOffspring", {"start": v(-55.38, 36.74) * mm, "end": v(-50.3, 36.74) * mm});
            skLineSegment(sketch, "E319.0", {"start": v(-42.68, 49.44) * mm, "end": v(-37.6, 49.44) * mm});
            skLineSegment(sketch, "E320.trimOffspring", {"start": v(-35.06, 46.9) * mm, "end": v(-35.06, 41.82) * mm});
            skLineSegment(sketch, "E321.trimOffspring", {"start": v(-68.08, 26.58) * mm, "end": v(-63, 26.58) * mm});
            skLineSegment(sketch, "E322.trimOffspring", {"start": v(-73.16, 21.5) * mm, "end": v(-73.16, 15.23) * mm});
            skLineSegment(sketch, "E323.trimOffspring", {"start": v(-70.62, 21.5) * mm, "end": v(-70.62, 15.23) * mm});
            skLineSegment(sketch, "E324.trimOffspring", {"start": v(-68.08, 24.04) * mm, "end": v(-63, 24.04) * mm});
            skLineSegment(sketch, "E325.0", {"start": v(-80.78, 10.15) * mm, "end": v(-75.7, 10.15) * mm});
            skLineSegment(sketch, "E326.trimOffspring", {"start": v(-83.32, 7.6) * mm, "end": v(-83.32, 2.59) * mm});
            skLineSegment(sketch, "E327.trimOffspring", {"start": v(-68.08, 12.69) * mm, "end": v(-63.62, 12.69) * mm});
            skLineSegment(sketch, "E328.trimOffspring", {"start": v(-68.08, 10.15) * mm, "end": v(-65.15, 10.15) * mm});
            skLineSegment(sketch, "E329.trimOffspring", {"start": v(-70.62, 7.6) * mm, "end": v(-70.62, 2.59) * mm});
            skLineSegment(sketch, "E330.trimOffspring", {"start": v(-73.16, 7.6) * mm, "end": v(-73.16, 2.59) * mm});
            skLineSegment(sketch, "E331.trimOffspring", {"start": v(-19.83, 33.04) * mm, "end": v(-19.83, 29.12) * mm});
            skLineSegment(sketch, "E332.trimOffspring", {"start": v(-22.37, 33.56) * mm, "end": v(-22.37, 29.12) * mm});
            skLineSegment(sketch, "E333.trimOffspring", {"start": v(-9.66, 30.97) * mm, "end": v(-9.66, 29.12) * mm});
            skLineSegment(sketch, "E334.trimOffspring", {"start": v(-7.12, 30.46) * mm, "end": v(-7.12, 29.12) * mm});
            skLineSegment(sketch, "E335.trimOffspring", {"start": v(3.04, 28.46) * mm, "end": v(3.04, 26.58) * mm});
            skLineSegment(sketch, "E336.trimOffspring", {"start": v(5.58, 27.96) * mm, "end": v(5.58, 26.58) * mm});
            skLineSegment(sketch, "E337.trimOffspring", {"start": v(8.12, 51.98) * mm, "end": v(13.42, 51.98) * mm});
            skArc(sketch, "E338.filletArc", {"start": v(-45.22, 41.82) * mm, "mid": v(-44.48, 40.02) * mm, "end": v(-42.68, 39.28) * mm});
            skPoint(sketch, "E339.visualSharp", {"position": v(-45.22, 49.44) * mm});
            skArc(sketch, "E339.filletArc", {"start": v(-42.68, 49.44) * mm, "mid": v(-44.48, 48.7) * mm, "end": v(-45.22, 46.9) * mm});
            skPoint(sketch, "E340.visualSharp", {"position": v(-35.06, 49.44) * mm});
            skArc(sketch, "E340.filletArc", {"start": v(-35.06, 46.9) * mm, "mid": v(-35.8, 48.7) * mm, "end": v(-37.6, 49.44) * mm});
            skPoint(sketch, "E341.visualSharp", {"position": v(-35.06, 39.28) * mm});
            skArc(sketch, "E341.filletArc", {"start": v(-37.6, 39.28) * mm, "mid": v(-35.8, 40.02) * mm, "end": v(-35.06, 41.82) * mm});
            skArc(sketch, "E342.filletArc", {"start": v(-42.68, 36.74) * mm, "mid": v(-44.48, 36) * mm, "end": v(-45.22, 34.2) * mm});
            skPoint(sketch, "E343.visualSharp", {"position": v(-35.06, 36.74) * mm});
            skArc(sketch, "E343.filletArc", {"start": v(-35.06, 34.2) * mm, "mid": v(-35.8, 36) * mm, "end": v(-37.6, 36.74) * mm});
            skArc(sketch, "E344.filletArc", {"start": v(-37.6, 26.58) * mm, "mid": v(-35.8, 27.32) * mm, "end": v(-35.06, 29.12) * mm});
            skPoint(sketch, "E345.visualSharp", {"position": v(-45.22, 26.58) * mm});
            skArc(sketch, "E345.filletArc", {"start": v(-45.22, 29.12) * mm, "mid": v(-44.48, 27.32) * mm, "end": v(-42.68, 26.58) * mm});
            skPoint(sketch, "E346.visualSharp", {"position": v(-47.76, 36.74) * mm});
            skArc(sketch, "E346.filletArc", {"start": v(-47.76, 34.2) * mm, "mid": v(-48.5, 36) * mm, "end": v(-50.3, 36.74) * mm});
            skPoint(sketch, "E347.visualSharp", {"position": v(-47.76, 39.28) * mm});
            skArc(sketch, "E347.filletArc", {"start": v(-50.3, 39.28) * mm, "mid": v(-48.5, 40.02) * mm, "end": v(-47.76, 41.82) * mm});
            skPoint(sketch, "E348.visualSharp", {"position": v(-47.76, 26.58) * mm});
            skArc(sketch, "E348.filletArc", {"start": v(-50.3, 26.58) * mm, "mid": v(-48.5, 27.32) * mm, "end": v(-47.76, 29.12) * mm});
            skPoint(sketch, "E349.visualSharp", {"position": v(-47.76, 24.04) * mm});
            skArc(sketch, "E350.filletArc", {"start": v(-32.52, 29.12) * mm, "mid": v(-31.78, 27.32) * mm, "end": v(-29.98, 26.58) * mm});
            skPoint(sketch, "E351.visualSharp", {"position": v(-32.52, 36.74) * mm});
            skArc(sketch, "E351.filletArc", {"start": v(-29.98, 36.74) * mm, "mid": v(-31.78, 36) * mm, "end": v(-32.52, 34.2) * mm});
            skArc(sketch, "E352.filletArc", {"start": v(-24.9, 26.58) * mm, "mid": v(-23.11, 27.32) * mm, "end": v(-22.37, 29.12) * mm});
            skArc(sketch, "E353.filletArc", {"start": v(-19.83, 29.12) * mm, "mid": v(-19.08, 27.32) * mm, "end": v(-17.29, 26.58) * mm});
            skArc(sketch, "E354.filletArc", {"start": v(-12.2, 26.58) * mm, "mid": v(-10.4, 27.32) * mm, "end": v(-9.66, 29.12) * mm});
            skArc(sketch, "E355.filletArc", {"start": v(-7.12, 29.12) * mm, "mid": v(-6.37, 27.32) * mm, "end": v(-4.58, 26.58) * mm});
            skArc(sketch, "E356.filletArc", {"start": v(-4.58, 24.04) * mm, "mid": v(-6.37, 23.3) * mm, "end": v(-7.12, 21.5) * mm});
            skArc(sketch, "E357.filletArc", {"start": v(-9.66, 21.5) * mm, "mid": v(-10.4, 23.3) * mm, "end": v(-12.2, 24.04) * mm});
            skPoint(sketch, "E358.visualSharp", {"position": v(3.04, 24.04) * mm});
            skArc(sketch, "E358.filletArc", {"start": v(3.04, 21.5) * mm, "mid": v(2.3, 23.3) * mm, "end": v(0.5, 24.04) * mm});
            skArc(sketch, "E359.filletArc", {"start": v(-17.29, 24.04) * mm, "mid": v(-19.08, 23.3) * mm, "end": v(-19.83, 21.5) * mm});
            skArc(sketch, "E360.filletArc", {"start": v(-22.37, 21.5) * mm, "mid": v(-23.11, 23.3) * mm, "end": v(-24.9, 24.04) * mm});
            skArc(sketch, "E361.filletArc", {"start": v(-29.98, 24.04) * mm, "mid": v(-31.78, 23.3) * mm, "end": v(-32.52, 21.5) * mm});
            skArc(sketch, "E362.filletArc", {"start": v(-35.06, 21.5) * mm, "mid": v(-35.8, 23.3) * mm, "end": v(-37.6, 24.04) * mm});
            skPoint(sketch, "E363.visualSharp", {"position": v(5.58, 24.04) * mm});
            skArc(sketch, "E363.filletArc", {"start": v(8.12, 24.04) * mm, "mid": v(6.32, 23.3) * mm, "end": v(5.58, 21.5) * mm});
            skArc(sketch, "E364.filletArc", {"start": v(15.7, 21.5) * mm, "mid": v(14.95, 23.3) * mm, "end": v(13.16, 24.04) * mm});
            skArc(sketch, "E365.filletArc", {"start": v(20.78, 24.04) * mm, "mid": v(18.98, 23.3) * mm, "end": v(18.24, 21.5) * mm});
            skPoint(sketch, "E366.visualSharp", {"position": v(-57.92, 39.28) * mm});
            skArc(sketch, "E366.filletArc", {"start": v(-57.92, 41.82) * mm, "mid": v(-57.18, 40.02) * mm, "end": v(-55.38, 39.28) * mm});
            skPoint(sketch, "E367.visualSharp", {"position": v(-57.92, 36.74) * mm});
            skArc(sketch, "E367.filletArc", {"start": v(-55.38, 36.74) * mm, "mid": v(-57.18, 36) * mm, "end": v(-57.92, 34.2) * mm});
            skPoint(sketch, "E368.visualSharp", {"position": v(-60.46, 36.74) * mm});
            skArc(sketch, "E368.filletArc", {"start": v(-60.46, 34.2) * mm, "mid": v(-61.2, 36) * mm, "end": v(-63, 36.74) * mm});
            skLineSegment(sketch, "E369.trimOffspring", {"start": v(-55.38, 26.58) * mm, "end": v(-50.3, 26.58) * mm});
            skLineSegment(sketch, "E370.trimOffspring", {"start": v(-57.92, 21.5) * mm, "end": v(-57.92, 18.43) * mm});
            skLineSegment(sketch, "E371.trimOffspring", {"start": v(-55.38, 24.04) * mm, "end": v(-49.28, 24.04) * mm});
            skLineSegment(sketch, "E372.trimOffspring", {"start": v(-60.46, 21.5) * mm, "end": v(-60.46, 16.35) * mm});
            skArc(sketch, "E373.filletArc", {"start": v(13.16, 12.69) * mm, "mid": v(14.95, 13.43) * mm, "end": v(15.7, 15.23) * mm});
            skPoint(sketch, "E374.visualSharp", {"position": v(30.97, 12.69) * mm});
            skArc(sketch, "E374.filletArc", {"start": v(30.97, 15.23) * mm, "mid": v(31.72, 13.43) * mm, "end": v(33.51, 12.69) * mm});
            skPoint(sketch, "E375.visualSharp", {"position": v(28.43, 12.69) * mm});
            skArc(sketch, "E375.filletArc", {"start": v(25.9, 12.69) * mm, "mid": v(27.69, 13.43) * mm, "end": v(28.43, 15.23) * mm});
            skArc(sketch, "E376.filletArc", {"start": v(18.24, 15.23) * mm, "mid": v(18.98, 13.43) * mm, "end": v(20.78, 12.69) * mm});
            skArc(sketch, "E377.filletArc", {"start": v(15.7, 7.6) * mm, "mid": v(14.95, 9.4) * mm, "end": v(13.16, 10.15) * mm});
            skPoint(sketch, "E378.visualSharp", {"position": v(41.13, 12.69) * mm});
            skArc(sketch, "E378.filletArc", {"start": v(38.6, 12.69) * mm, "mid": v(40.39, 13.43) * mm, "end": v(41.13, 15.23) * mm});
            skPoint(sketch, "E379.visualSharp", {"position": v(43.67, 12.69) * mm});
            skArc(sketch, "E379.filletArc", {"start": v(43.67, 15.23) * mm, "mid": v(44.41, 13.43) * mm, "end": v(46.21, 12.69) * mm});
            skArc(sketch, "E380.filletArc", {"start": v(51.3, 12.69) * mm, "mid": v(53.1, 13.43) * mm, "end": v(53.84, 15.23) * mm});
            skArc(sketch, "E381.filletArc", {"start": v(56.38, 15.23) * mm, "mid": v(57.12, 13.43) * mm, "end": v(58.92, 12.69) * mm});
            skPoint(sketch, "E382.visualSharp", {"position": v(56.38, 10.15) * mm});
            skArc(sketch, "E382.filletArc", {"start": v(58.92, 10.15) * mm, "mid": v(57.12, 9.4) * mm, "end": v(56.38, 7.6) * mm});
            skArc(sketch, "E383.filletArc", {"start": v(53.84, 7.6) * mm, "mid": v(53.1, 9.4) * mm, "end": v(51.3, 10.15) * mm});
            skPoint(sketch, "E384.visualSharp", {"position": v(43.67, 10.15) * mm});
            skArc(sketch, "E384.filletArc", {"start": v(46.21, 10.15) * mm, "mid": v(44.41, 9.4) * mm, "end": v(43.67, 7.6) * mm});
            skPoint(sketch, "E385.visualSharp", {"position": v(41.13, 10.15) * mm});
            skArc(sketch, "E385.filletArc", {"start": v(41.13, 7.6) * mm, "mid": v(40.39, 9.4) * mm, "end": v(38.6, 10.15) * mm});
            skPoint(sketch, "E386.visualSharp", {"position": v(30.97, 10.15) * mm});
            skArc(sketch, "E386.filletArc", {"start": v(33.51, 10.15) * mm, "mid": v(31.72, 9.4) * mm, "end": v(30.97, 7.6) * mm});
            skPoint(sketch, "E387.visualSharp", {"position": v(28.43, 10.15) * mm});
            skArc(sketch, "E387.filletArc", {"start": v(28.43, 7.6) * mm, "mid": v(27.69, 9.4) * mm, "end": v(25.9, 10.15) * mm});
            skArc(sketch, "E388.filletArc", {"start": v(20.78, 10.15) * mm, "mid": v(18.98, 9.4) * mm, "end": v(18.24, 7.6) * mm});
            skPoint(sketch, "E389.visualSharp", {"position": v(69.1, 10.15) * mm});
            skArc(sketch, "E389.filletArc", {"start": v(71.64, 10.15) * mm, "mid": v(69.84, 9.4) * mm, "end": v(69.1, 7.6) * mm});
            skPoint(sketch, "E390.visualSharp", {"position": v(66.56, 0) * mm});
            skArc(sketch, "E390.filletArc", {"start": v(64.02, 0) * mm, "mid": v(65.82, 0.75) * mm, "end": v(66.56, 2.54) * mm});
            skPoint(sketch, "E391.visualSharp", {"position": v(66.56, 10.15) * mm});
            skArc(sketch, "E391.filletArc", {"start": v(66.56, 7.6) * mm, "mid": v(65.82, 9.4) * mm, "end": v(64.02, 10.15) * mm});
            skPoint(sketch, "E392.visualSharp", {"position": v(81.5, 0) * mm});
            skArc(sketch, "E392.filletArc", {"start": v(81.5, 2.54) * mm, "mid": v(82.24, 0.75) * mm, "end": v(84.04, 0) * mm});
            skPoint(sketch, "E393.visualSharp", {"position": v(78.96, 0) * mm});
            skArc(sketch, "E393.filletArc", {"start": v(76.42, 0) * mm, "mid": v(78.22, 0.75) * mm, "end": v(78.96, 2.54) * mm});
            skPoint(sketch, "E394.visualSharp", {"position": v(78.96, 10.15) * mm});
            skArc(sketch, "E394.filletArc", {"start": v(78.96, 7.6) * mm, "mid": v(78.22, 9.4) * mm, "end": v(76.42, 10.15) * mm});
            skPoint(sketch, "E395.visualSharp", {"position": v(81.5, 10.15) * mm});
            skArc(sketch, "E395.filletArc", {"start": v(84.04, 10.15) * mm, "mid": v(82.25, 9.4) * mm, "end": v(81.5, 7.6) * mm});
            skPoint(sketch, "E396.visualSharp", {"position": v(69.1, 0) * mm});
            skArc(sketch, "E396.filletArc", {"start": v(69.1, 2.54) * mm, "mid": v(69.84, 0.75) * mm, "end": v(71.64, 0) * mm});
            skPoint(sketch, "E397.visualSharp", {"position": v(56.38, 0) * mm});
            skArc(sketch, "E397.filletArc", {"start": v(56.38, 2.54) * mm, "mid": v(57.12, 0.75) * mm, "end": v(58.92, 0) * mm});
            skPoint(sketch, "E398.visualSharp", {"position": v(66.56, 12.69) * mm});
            skArc(sketch, "E398.filletArc", {"start": v(64.02, 12.69) * mm, "mid": v(65.82, 13.43) * mm, "end": v(66.56, 15.23) * mm});
            skPoint(sketch, "E399.visualSharp", {"position": v(69.1, 12.69) * mm});
            skArc(sketch, "E399.filletArc", {"start": v(69.1, 15.23) * mm, "mid": v(69.84, 13.43) * mm, "end": v(71.64, 12.69) * mm});
            skPoint(sketch, "E400.visualSharp", {"position": v(78.96, 12.69) * mm});
            skArc(sketch, "E400.filletArc", {"start": v(76.42, 12.69) * mm, "mid": v(78.22, 13.43) * mm, "end": v(78.96, 15.23) * mm});
            skPoint(sketch, "E401.visualSharp", {"position": v(81.5, 12.69) * mm});
            skArc(sketch, "E401.filletArc", {"start": v(81.5, 15.23) * mm, "mid": v(82.25, 13.43) * mm, "end": v(84.04, 12.69) * mm});
            skPoint(sketch, "E402.visualSharp", {"position": v(81.5, 24.04) * mm});
            skArc(sketch, "E402.filletArc", {"start": v(84.04, 24.04) * mm, "mid": v(82.25, 23.3) * mm, "end": v(81.5, 21.5) * mm});
            skArc(sketch, "E403.filletArc", {"start": v(18.24, 2.53) * mm, "mid": v(18.98, 0.74) * mm, "end": v(20.78, 0) * mm});
            skArc(sketch, "E404.filletArc", {"start": v(25.9, 0) * mm, "mid": v(27.7, 0.74) * mm, "end": v(28.43, 2.54) * mm});
            skPoint(sketch, "E405.visualSharp", {"position": v(5.58, 12.69) * mm});
            skArc(sketch, "E405.filletArc", {"start": v(5.58, 15.23) * mm, "mid": v(6.32, 13.43) * mm, "end": v(8.12, 12.69) * mm});
            skPoint(sketch, "E406.visualSharp", {"position": v(3.04, 12.69) * mm});
            skArc(sketch, "E406.filletArc", {"start": v(0.5, 12.69) * mm, "mid": v(2.3, 13.43) * mm, "end": v(3.04, 15.23) * mm});
            skPoint(sketch, "E407.visualSharp", {"position": v(81.5, 33.53) * mm});
            skArc(sketch, "E407.filletArc", {"start": v(84.04, 33.53) * mm, "mid": v(82.25, 32.79) * mm, "end": v(81.5, 31) * mm});
            skPoint(sketch, "E408.visualSharp", {"position": v(81.5, 26.58) * mm});
            skArc(sketch, "E408.filletArc", {"start": v(81.5, 29.12) * mm, "mid": v(82.25, 27.33) * mm, "end": v(84.04, 26.58) * mm});
            skPoint(sketch, "E409.visualSharp", {"position": v(81.5, -2.54) * mm});
            skArc(sketch, "E409.filletArc", {"start": v(84.04, -2.54) * mm, "mid": v(82.24, -3.28) * mm, "end": v(81.5, -5.08) * mm});
            skPoint(sketch, "E410.visualSharp", {"position": v(81.5, -12.71) * mm});
            skArc(sketch, "E410.filletArc", {"start": v(81.5, -10.17) * mm, "mid": v(82.24, -11.97) * mm, "end": v(84.04, -12.71) * mm});
            skPoint(sketch, "E411.visualSharp", {"position": v(78.96, -2.54) * mm});
            skArc(sketch, "E411.filletArc", {"start": v(78.96, -5.08) * mm, "mid": v(78.22, -3.28) * mm, "end": v(76.42, -2.54) * mm});
            skPoint(sketch, "E412.visualSharp", {"position": v(81.5, -15.25) * mm});
            skArc(sketch, "E412.filletArc", {"start": v(84.04, -15.25) * mm, "mid": v(82.24, -16) * mm, "end": v(81.5, -17.8) * mm});
            skPoint(sketch, "E413.visualSharp", {"position": v(78.97, 35.54) * mm});
            skArc(sketch, "E413.filletArc", {"start": v(78.96, 33) * mm, "mid": v(78.22, 34.8) * mm, "end": v(76.42, 35.54) * mm});
            skPoint(sketch, "E414.visualSharp", {"position": v(69.36, 35.54) * mm});
            skArc(sketch, "E414.filletArc", {"start": v(71.73, 35.54) * mm, "mid": v(70, 34.85) * mm, "end": v(69.2, 33.18) * mm});
            skPoint(sketch, "E415.visualSharp", {"position": v(81.5, -25.41) * mm});
            skArc(sketch, "E415.filletArc", {"start": v(81.5, -22.87) * mm, "mid": v(82.24, -24.67) * mm, "end": v(84.04, -25.41) * mm});
            skPoint(sketch, "E416.visualSharp", {"position": v(81.5, -27.95) * mm});
            skArc(sketch, "E416.filletArc", {"start": v(84.04, -27.95) * mm, "mid": v(82.24, -28.7) * mm, "end": v(81.5, -30.5) * mm});
            skPoint(sketch, "E417.visualSharp", {"position": v(78.96, -27.95) * mm});
            skArc(sketch, "E417.filletArc", {"start": v(78.96, -30.5) * mm, "mid": v(78.21, -28.7) * mm, "end": v(76.42, -27.95) * mm});
            skPoint(sketch, "E418.visualSharp", {"position": v(69.03, -27.95) * mm});
            skArc(sketch, "E418.filletArc", {"start": v(71.57, -27.95) * mm, "mid": v(69.78, -28.7) * mm, "end": v(69.03, -30.5) * mm});
            skPoint(sketch, "E419.visualSharp", {"position": v(69.03, -38.11) * mm});
            skArc(sketch, "E419.filletArc", {"start": v(69.03, -35.57) * mm, "mid": v(69.78, -37.37) * mm, "end": v(71.57, -38.11) * mm});
            skPoint(sketch, "E420.visualSharp", {"position": v(78.96, -38.11) * mm});
            skArc(sketch, "E420.filletArc", {"start": v(76.42, -38.11) * mm, "mid": v(78.21, -37.37) * mm, "end": v(78.96, -35.57) * mm});
            skPoint(sketch, "E421.visualSharp", {"position": v(78.96, -25.41) * mm});
            skArc(sketch, "E421.filletArc", {"start": v(76.42, -25.41) * mm, "mid": v(78.21, -24.67) * mm, "end": v(78.96, -22.87) * mm});
            skPoint(sketch, "E422.visualSharp", {"position": v(69.03, -25.41) * mm});
            skArc(sketch, "E422.filletArc", {"start": v(69.03, -22.87) * mm, "mid": v(69.78, -24.67) * mm, "end": v(71.57, -25.41) * mm});
            skPoint(sketch, "E423.visualSharp", {"position": v(56.38, -25.41) * mm});
            skArc(sketch, "E423.filletArc", {"start": v(56.38, -22.87) * mm, "mid": v(57.12, -24.67) * mm, "end": v(58.92, -25.41) * mm});
            skPoint(sketch, "E424.visualSharp", {"position": v(66.5, -25.41) * mm});
            skArc(sketch, "E424.filletArc", {"start": v(63.95, -25.41) * mm, "mid": v(65.75, -24.67) * mm, "end": v(66.5, -22.87) * mm});
            skPoint(sketch, "E425.visualSharp", {"position": v(66.5, -27.95) * mm});
            skArc(sketch, "E425.filletArc", {"start": v(66.5, -30.5) * mm, "mid": v(65.75, -28.7) * mm, "end": v(63.95, -27.95) * mm});
            skPoint(sketch, "E426.visualSharp", {"position": v(66.5, -38.11) * mm});
            skArc(sketch, "E426.filletArc", {"start": v(63.95, -38.11) * mm, "mid": v(65.75, -37.37) * mm, "end": v(66.5, -35.57) * mm});
            skPoint(sketch, "E427.visualSharp", {"position": v(66.5, -40.65) * mm});
            skArc(sketch, "E427.filletArc", {"start": v(66.5, -43.2) * mm, "mid": v(65.75, -41.4) * mm, "end": v(63.95, -40.65) * mm});
            skPoint(sketch, "E428.visualSharp", {"position": v(69.03, -40.65) * mm});
            skArc(sketch, "E428.filletArc", {"start": v(71.57, -40.65) * mm, "mid": v(69.78, -41.4) * mm, "end": v(69.03, -43.2) * mm});
            skPoint(sketch, "E429.visualSharp", {"position": v(53.84, -27.95) * mm});
            skArc(sketch, "E429.filletArc", {"start": v(53.84, -30.5) * mm, "mid": v(53.1, -28.7) * mm, "end": v(51.3, -27.95) * mm});
            skPoint(sketch, "E430.visualSharp", {"position": v(53.84, -25.41) * mm});
            skArc(sketch, "E430.filletArc", {"start": v(51.3, -25.41) * mm, "mid": v(53.1, -24.67) * mm, "end": v(53.84, -22.87) * mm});
            skPoint(sketch, "E431.visualSharp", {"position": v(43.67, -25.41) * mm});
            skArc(sketch, "E431.filletArc", {"start": v(43.67, -22.87) * mm, "mid": v(44.41, -24.67) * mm, "end": v(46.21, -25.41) * mm});
            skPoint(sketch, "E432.visualSharp", {"position": v(41.13, -25.41) * mm});
            skArc(sketch, "E432.filletArc", {"start": v(38.6, -25.41) * mm, "mid": v(40.39, -24.67) * mm, "end": v(41.13, -22.87) * mm});
            skArc(sketch, "E433.filletArc", {"start": v(41.13, -17.8) * mm, "mid": v(40.39, -16) * mm, "end": v(38.6, -15.25) * mm});
            skPoint(sketch, "E434.visualSharp", {"position": v(30.97, -15.25) * mm});
            skArc(sketch, "E434.filletArc", {"start": v(33.51, -15.25) * mm, "mid": v(31.72, -16) * mm, "end": v(30.97, -17.8) * mm});
            skPoint(sketch, "E435.visualSharp", {"position": v(28.43, -25.41) * mm});
            skArc(sketch, "E435.filletArc", {"start": v(25.9, -25.41) * mm, "mid": v(27.7, -24.67) * mm, "end": v(28.43, -22.87) * mm});
            skPoint(sketch, "E436.visualSharp", {"position": v(30.97, -25.41) * mm});
            skArc(sketch, "E436.filletArc", {"start": v(30.97, -22.87) * mm, "mid": v(31.72, -24.67) * mm, "end": v(33.51, -25.41) * mm});
            skPoint(sketch, "E437.visualSharp", {"position": v(28.43, -15.25) * mm});
            skArc(sketch, "E437.filletArc", {"start": v(28.43, -17.8) * mm, "mid": v(27.69, -16) * mm, "end": v(25.9, -15.25) * mm});
            skPoint(sketch, "E438.visualSharp", {"position": v(56.38, -27.95) * mm});
            skArc(sketch, "E438.filletArc", {"start": v(58.92, -27.95) * mm, "mid": v(57.12, -28.7) * mm, "end": v(56.38, -30.5) * mm});
            skPoint(sketch, "E439.visualSharp", {"position": v(69.03, -50.81) * mm});
            skArc(sketch, "E439.filletArc", {"start": v(69.03, -48.27) * mm, "mid": v(69.78, -50.07) * mm, "end": v(71.57, -50.81) * mm});
            skPoint(sketch, "E440.visualSharp", {"position": v(66.5, -50.81) * mm});
            skArc(sketch, "E440.filletArc", {"start": v(63.95, -50.81) * mm, "mid": v(65.75, -50.07) * mm, "end": v(66.5, -48.27) * mm});
            skPoint(sketch, "E441.visualSharp", {"position": v(66.5, -53.35) * mm});
            skArc(sketch, "E441.filletArc", {"start": v(66.5, -55.9) * mm, "mid": v(65.75, -54.1) * mm, "end": v(63.95, -53.35) * mm});
            skPoint(sketch, "E442.visualSharp", {"position": v(18.24, -15.25) * mm});
            skArc(sketch, "E442.filletArc", {"start": v(20.78, -15.25) * mm, "mid": v(18.98, -16) * mm, "end": v(18.24, -17.8) * mm});
            skPoint(sketch, "E443.visualSharp", {"position": v(15.7, -15.25) * mm});
            skArc(sketch, "E443.filletArc", {"start": v(15.7, -17.8) * mm, "mid": v(14.95, -16) * mm, "end": v(13.16, -15.25) * mm});
            skPoint(sketch, "E444.visualSharp", {"position": v(3.04, -15.25) * mm});
            skArc(sketch, "E444.filletArc", {"start": v(3.04, -17.8) * mm, "mid": v(2.3, -16) * mm, "end": v(0.5, -15.25) * mm});
            skPoint(sketch, "E445.visualSharp", {"position": v(5.58, -15.25) * mm});
            skArc(sketch, "E445.filletArc", {"start": v(8.12, -15.25) * mm, "mid": v(6.32, -16) * mm, "end": v(5.58, -17.8) * mm});
            skLineSegment(sketch, "E446", {"start": v(18.19, -10.22) * mm, "end": v(18.08, -4.38) * mm});
            skPoint(sketch, "E447.visualSharp", {"position": v(18.24, -12.71) * mm});
            skArc(sketch, "E447.filletArc", {"start": v(18.19, -10.22) * mm, "mid": v(18.95, -11.98) * mm, "end": v(20.73, -12.71) * mm});
            skPoint(sketch, "E448.visualSharp", {"position": v(15.7, -12.71) * mm});
            skArc(sketch, "E448.filletArc", {"start": v(13.16, -12.71) * mm, "mid": v(14.95, -11.97) * mm, "end": v(15.7, -10.17) * mm});
            skPoint(sketch, "E449.visualSharp", {"position": v(43.67, -27.95) * mm});
            skArc(sketch, "E449.filletArc", {"start": v(46.21, -27.95) * mm, "mid": v(44.41, -28.7) * mm, "end": v(43.67, -30.5) * mm});
            skPoint(sketch, "E450.visualSharp", {"position": v(-35.06, 51.98) * mm});
            skArc(sketch, "E450.filletArc", {"start": v(-37.6, 51.98) * mm, "mid": v(-35.8, 52.72) * mm, "end": v(-35.06, 54.52) * mm});
            skPoint(sketch, "E451.visualSharp", {"position": v(-32.52, 51.98) * mm});
            skPoint(sketch, "E452.visualSharp", {"position": v(-70.62, 26.58) * mm});
            skArc(sketch, "E452.filletArc", {"start": v(-70.62, 29.12) * mm, "mid": v(-69.88, 27.32) * mm, "end": v(-68.08, 26.58) * mm});
            skPoint(sketch, "E453.visualSharp", {"position": v(-60.46, 26.58) * mm});
            skArc(sketch, "E453.filletArc", {"start": v(-63, 26.58) * mm, "mid": v(-61.2, 27.32) * mm, "end": v(-60.46, 29.12) * mm});
            skPoint(sketch, "E454.visualSharp", {"position": v(-70.62, 24.04) * mm});
            skArc(sketch, "E454.filletArc", {"start": v(-68.08, 24.04) * mm, "mid": v(-69.88, 23.3) * mm, "end": v(-70.62, 21.5) * mm});
            skPoint(sketch, "E455.visualSharp", {"position": v(-60.46, 24.04) * mm});
            skArc(sketch, "E455.filletArc", {"start": v(-60.46, 21.5) * mm, "mid": v(-61.2, 23.3) * mm, "end": v(-63, 24.04) * mm});
            skPoint(sketch, "E456.visualSharp", {"position": v(-57.92, 24.04) * mm});
            skArc(sketch, "E456.filletArc", {"start": v(-55.38, 24.04) * mm, "mid": v(-57.18, 23.3) * mm, "end": v(-57.92, 21.5) * mm});
            skArc(sketch, "E457", {"start": v(-44, 24.04) * mm, "mid": v(-44.87, 23.58) * mm, "end": v(-45.22, 22.65) * mm});
            skArc(sketch, "E458", {"start": v(-47.76, 22.44) * mm, "mid": v(-48.2, 23.54) * mm, "end": v(-49.28, 24.04) * mm});
            skArc(sketch, "E459", {"start": v(-32.52, 53.86) * mm, "mid": v(-31.75, 52.51) * mm, "end": v(-30.3, 51.98) * mm});
            skArc(sketch, "E460", {"start": v(-47.76, 48.9) * mm, "mid": v(-48.83, 49.83) * mm, "end": v(-50.22, 49.6) * mm});
            skPoint(sketch, "E461.visualSharp", {"position": v(-73.16, 24.04) * mm});
            skArc(sketch, "E461.filletArc", {"start": v(-73.16, 21.5) * mm, "mid": v(-73.9, 23.3) * mm, "end": v(-75.7, 24.04) * mm});
            skPoint(sketch, "E462.visualSharp", {"position": v(-70.62, 12.69) * mm});
            skArc(sketch, "E462.filletArc", {"start": v(-70.62, 15.23) * mm, "mid": v(-69.88, 13.43) * mm, "end": v(-68.08, 12.69) * mm});
            skPoint(sketch, "E463.visualSharp", {"position": v(-73.16, 12.69) * mm});
            skArc(sketch, "E463.filletArc", {"start": v(-75.7, 12.69) * mm, "mid": v(-73.9, 13.43) * mm, "end": v(-73.16, 15.23) * mm});
            skPoint(sketch, "E464.visualSharp", {"position": v(-57.92, 26.58) * mm});
            skArc(sketch, "E464.filletArc", {"start": v(-57.92, 29.12) * mm, "mid": v(-57.18, 27.32) * mm, "end": v(-55.38, 26.58) * mm});
            skPoint(sketch, "E465.visualSharp", {"position": v(-83.32, 10.15) * mm});
            skArc(sketch, "E465.filletArc", {"start": v(-80.78, 10.15) * mm, "mid": v(-82.58, 9.4) * mm, "end": v(-83.32, 7.6) * mm});
            skPoint(sketch, "E466.visualSharp", {"position": v(-73.16, 10.15) * mm});
            skArc(sketch, "E466.filletArc", {"start": v(-73.16, 7.6) * mm, "mid": v(-73.9, 9.4) * mm, "end": v(-75.7, 10.15) * mm});
            skPoint(sketch, "E467.visualSharp", {"position": v(-70.62, 10.15) * mm});
            skArc(sketch, "E467.filletArc", {"start": v(-68.08, 10.15) * mm, "mid": v(-69.88, 9.4) * mm, "end": v(-70.62, 7.6) * mm});
            skPoint(sketch, "E468.visualSharp", {"position": v(-70.62, 0.05) * mm});
            skArc(sketch, "E468.filletArc", {"start": v(-70.62, 2.59) * mm, "mid": v(-69.88, 0.8) * mm, "end": v(-68.08, 0.05) * mm});
            skPoint(sketch, "E469.visualSharp", {"position": v(-73.16, 0.05) * mm});
            skArc(sketch, "E469.filletArc", {"start": v(-75.7, 0.05) * mm, "mid": v(-73.9, 0.8) * mm, "end": v(-73.16, 2.59) * mm});
            skPoint(sketch, "E470.visualSharp", {"position": v(-83.32, 0.05) * mm});
            skArc(sketch, "E470.filletArc", {"start": v(-83.32, 2.59) * mm, "mid": v(-82.58, 0.8) * mm, "end": v(-80.78, 0.05) * mm});
            skPoint(sketch, "E471.visualSharp", {"position": v(-85.86, 0.05) * mm});
            skArc(sketch, "E471.filletArc", {"start": v(-88.4, 0.05) * mm, "mid": v(-86.6, 0.8) * mm, "end": v(-85.86, 2.59) * mm});
            skArc(sketch, "E472", {"start": v(-83.32, 14.04) * mm, "mid": v(-82.95, 13.1) * mm, "end": v(-82.04, 12.69) * mm});
            skPoint(sketch, "E473.visualSharp", {"position": v(-83.32, -2.5) * mm});
            skArc(sketch, "E473.filletArc", {"start": v(-80.78, -2.5) * mm, "mid": v(-82.58, -3.24) * mm, "end": v(-83.32, -5.03) * mm});
            skPoint(sketch, "E474.visualSharp", {"position": v(-70.62, -2.5) * mm});
            skArc(sketch, "E474.filletArc", {"start": v(-68.08, -2.5) * mm, "mid": v(-69.88, -3.24) * mm, "end": v(-70.62, -5.03) * mm});
            skPoint(sketch, "E475.visualSharp", {"position": v(-70.62, -12.71) * mm});
            skArc(sketch, "E475.filletArc", {"start": v(-70.62, -10.17) * mm, "mid": v(-69.88, -11.97) * mm, "end": v(-68.08, -12.71) * mm});
            skPoint(sketch, "E476.visualSharp", {"position": v(-73.16, -12.71) * mm});
            skArc(sketch, "E476.filletArc", {"start": v(-75.7, -12.71) * mm, "mid": v(-73.9, -11.97) * mm, "end": v(-73.16, -10.17) * mm});
            skPoint(sketch, "E477.visualSharp", {"position": v(-73.16, -2.5) * mm});
            skArc(sketch, "E477.filletArc", {"start": v(-73.16, -5.03) * mm, "mid": v(-73.9, -3.24) * mm, "end": v(-75.7, -2.5) * mm});
            skPoint(sketch, "E478.visualSharp", {"position": v(-83.32, -12.71) * mm});
            skArc(sketch, "E478.filletArc", {"start": v(-83.32, -10.17) * mm, "mid": v(-82.58, -11.97) * mm, "end": v(-80.78, -12.71) * mm});
            skPoint(sketch, "E479.visualSharp", {"position": v(-85.86, -12.71) * mm});
            skArc(sketch, "E479.filletArc", {"start": v(-88.4, -12.71) * mm, "mid": v(-86.6, -11.97) * mm, "end": v(-85.86, -10.17) * mm});
            skPoint(sketch, "E480.visualSharp", {"position": v(-85.86, -2.5) * mm});
            skArc(sketch, "E480.filletArc", {"start": v(-85.86, -5.03) * mm, "mid": v(-86.6, -3.24) * mm, "end": v(-88.4, -2.5) * mm});
            skPoint(sketch, "E481.visualSharp", {"position": v(-85.86, -15.25) * mm});
            skArc(sketch, "E481.filletArc", {"start": v(-85.86, -17.8) * mm, "mid": v(-86.6, -16) * mm, "end": v(-88.4, -15.25) * mm});
            skPoint(sketch, "E482.visualSharp", {"position": v(-85.86, -25.41) * mm});
            skArc(sketch, "E482.filletArc", {"start": v(-88.4, -25.41) * mm, "mid": v(-86.6, -24.67) * mm, "end": v(-85.86, -22.87) * mm});
            skPoint(sketch, "E483.visualSharp", {"position": v(-83.32, -15.25) * mm});
            skArc(sketch, "E483.filletArc", {"start": v(-80.78, -15.25) * mm, "mid": v(-82.58, -16) * mm, "end": v(-83.32, -17.8) * mm});
            skPoint(sketch, "E484.visualSharp", {"position": v(-73.16, -15.25) * mm});
            skArc(sketch, "E484.filletArc", {"start": v(-73.16, -17.8) * mm, "mid": v(-73.9, -16) * mm, "end": v(-75.7, -15.25) * mm});
            skPoint(sketch, "E485.visualSharp", {"position": v(-70.62, -15.25) * mm});
            skArc(sketch, "E485.filletArc", {"start": v(-68.08, -15.25) * mm, "mid": v(-69.88, -16) * mm, "end": v(-70.62, -17.8) * mm});
            skPoint(sketch, "E486.visualSharp", {"position": v(-70.62, -25.41) * mm});
            skArc(sketch, "E486.filletArc", {"start": v(-70.62, -22.87) * mm, "mid": v(-69.88, -24.67) * mm, "end": v(-68.08, -25.41) * mm});
            skPoint(sketch, "E487.visualSharp", {"position": v(-73.16, -25.41) * mm});
            skArc(sketch, "E487.filletArc", {"start": v(-75.7, -25.41) * mm, "mid": v(-73.9, -24.67) * mm, "end": v(-73.16, -22.87) * mm});
            skPoint(sketch, "E488.visualSharp", {"position": v(-83.32, -25.41) * mm});
            skArc(sketch, "E488.filletArc", {"start": v(-83.32, -22.87) * mm, "mid": v(-82.58, -24.67) * mm, "end": v(-80.78, -25.41) * mm});
            skPoint(sketch, "E489.visualSharp", {"position": v(-73.16, -27.95) * mm});
            skArc(sketch, "E489.filletArc", {"start": v(-73.16, -30.5) * mm, "mid": v(-73.9, -28.7) * mm, "end": v(-75.7, -27.95) * mm});
            skPoint(sketch, "E490.visualSharp", {"position": v(-83.32, -27.95) * mm});
            skArc(sketch, "E490.filletArc", {"start": v(-80.78, -27.95) * mm, "mid": v(-82.58, -28.7) * mm, "end": v(-83.32, -30.5) * mm});
            skPoint(sketch, "E491.visualSharp", {"position": v(-85.86, -27.95) * mm});
            skArc(sketch, "E491.filletArc", {"start": v(-85.86, -30.5) * mm, "mid": v(-86.6, -28.7) * mm, "end": v(-88.4, -27.95) * mm});
            skLineSegment(sketch, "E492.0", {"start": v(-60.46, -17.39) * mm, "end": v(-60.46, -22.87) * mm});
            skLineSegment(sketch, "E493.trimOffspring", {"start": v(-55.38, -25.41) * mm, "end": v(-49.23, -25.41) * mm});
            skLineSegment(sketch, "E494.trimOffspring", {"start": v(-57.92, -30.5) * mm, "end": v(-57.92, -37.24) * mm});
            skLineSegment(sketch, "E495.trimOffspring", {"start": v(-55.38, -27.95) * mm, "end": v(-50.3, -27.95) * mm});
            skLineSegment(sketch, "E496.0", {"start": v(-35.06, -21.94) * mm, "end": v(-35.06, -22.87) * mm});
            skLineSegment(sketch, "E497.0", {"start": v(-22.36, -19.3) * mm, "end": v(-22.36, -22.87) * mm});
            skPoint(sketch, "E498.visualSharp", {"position": v(-70.62, -27.95) * mm});
            skArc(sketch, "E498.filletArc", {"start": v(-68.08, -27.95) * mm, "mid": v(-69.88, -28.7) * mm, "end": v(-70.62, -30.5) * mm});
            skPoint(sketch, "E499.visualSharp", {"position": v(-60.46, -25.41) * mm});
            skArc(sketch, "E499.filletArc", {"start": v(-63, -25.41) * mm, "mid": v(-61.2, -24.67) * mm, "end": v(-60.46, -22.87) * mm});
            skPoint(sketch, "E500.visualSharp", {"position": v(-57.92, -25.41) * mm});
            skArc(sketch, "E500.filletArc", {"start": v(-57.92, -22.87) * mm, "mid": v(-57.18, -24.67) * mm, "end": v(-55.38, -25.41) * mm});
            skPoint(sketch, "E501.visualSharp", {"position": v(-57.92, -27.95) * mm});
            skArc(sketch, "E501.filletArc", {"start": v(-55.38, -27.95) * mm, "mid": v(-57.18, -28.7) * mm, "end": v(-57.92, -30.5) * mm});
            skLineSegment(sketch, "E502.trimOffspring", {"start": v(-42.68, -27.95) * mm, "end": v(-37.6, -27.95) * mm});
            skLineSegment(sketch, "E503.trimOffspring", {"start": v(-45.22, -30.5) * mm, "end": v(-45.22, -35.58) * mm});
            skLineSegment(sketch, "E504.trimOffspring", {"start": v(-35.06, -30.5) * mm, "end": v(-35.06, -33.7) * mm});
            skLineSegment(sketch, "E505.trimOffspring", {"start": v(-29.98, -27.95) * mm, "end": v(-24.9, -27.95) * mm});
            skLineSegment(sketch, "E506.trimOffspring", {"start": v(-29.98, -25.41) * mm, "end": v(-24.9, -25.41) * mm});
            skLineSegment(sketch, "E507.trimOffspring", {"start": v(-32.52, -30.5) * mm, "end": v(-32.52, -33.16) * mm});
            skLineSegment(sketch, "E508.trimOffspring", {"start": v(-17.29, -25.41) * mm, "end": v(-11.9, -25.41) * mm});
            skLineSegment(sketch, "E509.trimOffspring", {"start": v(-18.13, -27.95) * mm, "end": v(-13.12, -27.95) * mm});
            skLineSegment(sketch, "E510.trimOffspring", {"start": v(-22.36, -30.5) * mm, "end": v(-22.36, -30.67) * mm});
            skPoint(sketch, "E511.visualSharp", {"position": v(-47.76, -27.95) * mm});
            skArc(sketch, "E511.filletArc", {"start": v(-47.76, -30.5) * mm, "mid": v(-48.5, -28.7) * mm, "end": v(-50.3, -27.95) * mm});
            skLineSegment(sketch, "E512.trimOffspring", {"start": v(-43.57, -25.41) * mm, "end": v(-37.6, -25.41) * mm});
            skPoint(sketch, "E513.visualSharp", {"position": v(-60.46, -27.95) * mm});
            skArc(sketch, "E513.filletArc", {"start": v(-60.46, -30.5) * mm, "mid": v(-61.2, -28.7) * mm, "end": v(-63, -27.95) * mm});
            skLineSegment(sketch, "E514.trimOffspring", {"start": v(-47.76, -30.5) * mm, "end": v(-47.76, -35.97) * mm});
            skPoint(sketch, "E515.visualSharp", {"position": v(-45.22, -27.95) * mm});
            skArc(sketch, "E515.filletArc", {"start": v(-42.68, -27.95) * mm, "mid": v(-44.48, -28.7) * mm, "end": v(-45.22, -30.5) * mm});
            skPoint(sketch, "E516.visualSharp", {"position": v(-32.52, -25.41) * mm});
            skArc(sketch, "E516.filletArc", {"start": v(-32.52, -22.87) * mm, "mid": v(-31.78, -24.67) * mm, "end": v(-29.98, -25.41) * mm});
            skPoint(sketch, "E517.visualSharp", {"position": v(-32.52, -27.95) * mm});
            skArc(sketch, "E517.filletArc", {"start": v(-29.98, -27.95) * mm, "mid": v(-31.78, -28.7) * mm, "end": v(-32.52, -30.5) * mm});
            skPoint(sketch, "E518.visualSharp", {"position": v(-35.06, -27.95) * mm});
            skArc(sketch, "E518.filletArc", {"start": v(-35.06, -30.5) * mm, "mid": v(-35.8, -28.7) * mm, "end": v(-37.6, -27.95) * mm});
            skPoint(sketch, "E519.visualSharp", {"position": v(-22.36, -25.41) * mm});
            skArc(sketch, "E519.filletArc", {"start": v(-24.9, -25.41) * mm, "mid": v(-23.1, -24.67) * mm, "end": v(-22.36, -22.87) * mm});
            skPoint(sketch, "E520.visualSharp", {"position": v(-19.83, -25.41) * mm});
            skArc(sketch, "E520.filletArc", {"start": v(-19.83, -22.87) * mm, "mid": v(-19.08, -24.67) * mm, "end": v(-17.29, -25.41) * mm});
            skPoint(sketch, "E521.visualSharp", {"position": v(-22.36, -27.95) * mm});
            skArc(sketch, "E521.filletArc", {"start": v(-22.36, -30.5) * mm, "mid": v(-23.1, -28.7) * mm, "end": v(-24.9, -27.95) * mm});
            skPoint(sketch, "E522.visualSharp", {"position": v(-35.06, -25.41) * mm});
            skArc(sketch, "E522.filletArc", {"start": v(-37.6, -25.41) * mm, "mid": v(-35.8, -24.67) * mm, "end": v(-35.06, -22.87) * mm});
            skArc(sketch, "E523", {"start": v(-49.23, -25.41) * mm, "mid": v(-48.17, -24.69) * mm, "end": v(-47.76, -23.47) * mm});
            skArc(sketch, "E524", {"start": v(-45.22, -23.68) * mm, "mid": v(-44.74, -24.88) * mm, "end": v(-43.57, -25.41) * mm});
            skLineSegment(sketch, "E525.0", {"start": v(-88.64, -40.65) * mm, "end": v(-88.4, -40.65) * mm});
            skLineSegment(sketch, "E526.trimOffspring", {"start": v(-85.86, -43.2) * mm, "end": v(-85.86, -47.1) * mm});
            skLineSegment(sketch, "E527.trimOffspring", {"start": v(-83.32, -43.2) * mm, "end": v(-83.32, -48.27) * mm});
            skLineSegment(sketch, "E528.trimOffspring", {"start": v(-80.78, -38.11) * mm, "end": v(-75.33, -38.11) * mm});
            skLineSegment(sketch, "E529.trimOffspring", {"start": v(-80.78, -40.65) * mm, "end": v(-78.66, -40.65) * mm});
            skPoint(sketch, "E530.visualSharp", {"position": v(-85.86, -38.11) * mm});
            skArc(sketch, "E530.filletArc", {"start": v(-88.4, -38.11) * mm, "mid": v(-86.6, -37.37) * mm, "end": v(-85.86, -35.57) * mm});
            skPoint(sketch, "E531.visualSharp", {"position": v(-83.32, -38.11) * mm});
            skArc(sketch, "E531.filletArc", {"start": v(-83.32, -35.57) * mm, "mid": v(-82.58, -37.37) * mm, "end": v(-80.78, -38.11) * mm});
            skPoint(sketch, "E532.visualSharp", {"position": v(-83.32, -40.65) * mm});
            skArc(sketch, "E532.filletArc", {"start": v(-80.78, -40.65) * mm, "mid": v(-82.58, -41.4) * mm, "end": v(-83.32, -43.2) * mm});
            skPoint(sketch, "E533.visualSharp", {"position": v(-85.86, -40.65) * mm});
            skArc(sketch, "E533.filletArc", {"start": v(-85.86, -43.2) * mm, "mid": v(-86.6, -41.4) * mm, "end": v(-88.4, -40.65) * mm});
            skLineSegment(sketch, "E534.0", {"start": v(-82.4, -53.35) * mm, "end": v(-75.7, -53.35) * mm});
            skPoint(sketch, "E535.visualSharp", {"position": v(-83.32, -50.81) * mm});
            skArc(sketch, "E535.filletArc", {"start": v(-83.32, -48.27) * mm, "mid": v(-82.58, -50.07) * mm, "end": v(-80.78, -50.81) * mm});
            skLineSegment(sketch, "E536.trimOffspring", {"start": v(-73.16, -55.9) * mm, "end": v(-73.16, -62.47) * mm});
            skPoint(sketch, "E537.visualSharp", {"position": v(-73.16, -53.35) * mm});
            skArc(sketch, "E537.filletArc", {"start": v(-73.16, -55.9) * mm, "mid": v(-73.9, -54.1) * mm, "end": v(-75.7, -53.35) * mm});
            skArc(sketch, "E538", {"start": v(-68.36, -53.35) * mm, "mid": v(-69.99, -54.04) * mm, "end": v(-70.62, -55.7) * mm});
            skArc(sketch, "E539", {"start": v(-74.06, -50.81) * mm, "mid": v(-73.47, -50.61) * mm, "end": v(-73.16, -50.07) * mm});
            skArc(sketch, "E540", {"start": v(-18.13, -27.95) * mm, "mid": v(-19.35, -28.65) * mm, "end": v(-19.83, -29.96) * mm});
            skLineSegment(sketch, "E541.0", {"start": v(-60.46, -54.13) * mm, "end": v(-60.46, -58.17) * mm});
            skLineSegment(sketch, "E542.0", {"start": v(-47.76, -50.35) * mm, "end": v(-47.76, -54.28) * mm});
            skLineSegment(sketch, "E543.0", {"start": v(-35.06, -47.66) * mm, "end": v(-35.06, -51.53) * mm});
            skLineSegment(sketch, "E544.0", {"start": v(-22.36, -46.02) * mm, "end": v(-22.36, -49.84) * mm});
            skLineSegment(sketch, "E545.0", {"start": v(-9.67, -45.39) * mm, "end": v(-9.67, -49.2) * mm});
            skArc(sketch, "E546.trimOffspring", {"start": v(-7.12, -49.2) * mm, "mid": v(-39.32, -52.33) * mm, "end": v(-70.2, -61.97) * mm});
            skLineSegment(sketch, "E547.0", {"start": v(15.74, -47.14) * mm, "end": v(15.74, -50.99) * mm});
            skLineSegment(sketch, "E548.0", {"start": v(28.4, -49.54) * mm, "end": v(28.4, -53.45) * mm});
            skLineSegment(sketch, "E549.trimOffspring", {"start": v(41.13, -53.04) * mm, "end": v(41.13, -57.04) * mm});
            skLineSegment(sketch, "E550.trimOffspring", {"start": v(53.83, -57.56) * mm, "end": v(53.83, -61.82) * mm});
            skPoint(sketch, "E551.visualSharp", {"position": v(66.82, 35.54) * mm});
            skArc(sketch, "E551.filletArc", {"start": v(66.63, 32.82) * mm, "mid": v(65.95, 34.73) * mm, "end": v(64.1, 35.54) * mm});
            skPoint(sketch, "E552.visualSharp", {"position": v(67.08, 39.28) * mm});
            skArc(sketch, "E552.filletArc", {"start": v(64.72, 39.28) * mm, "mid": v(66.45, 39.96) * mm, "end": v(67.25, 41.64) * mm});
            skPoint(sketch, "E553.visualSharp", {"position": v(69.63, 39.28) * mm});
            skArc(sketch, "E553.filletArc", {"start": v(69.67, 39.82) * mm, "mid": v(69.8, 39.44) * mm, "end": v(70.17, 39.28) * mm});
            skPoint(sketch, "E554.visualSharp", {"position": v(56.19, 39.28) * mm});
            skArc(sketch, "E554.filletArc", {"start": v(56.19, 41.82) * mm, "mid": v(56.93, 40.03) * mm, "end": v(58.73, 39.28) * mm});
            skPoint(sketch, "E555.visualSharp", {"position": v(53.65, 39.28) * mm});
            skArc(sketch, "E555.filletArc", {"start": v(51.1, 39.28) * mm, "mid": v(52.9, 40.03) * mm, "end": v(53.65, 41.82) * mm});
            skPoint(sketch, "E556.visualSharp", {"position": v(5.58, 51.98) * mm});
            skArc(sketch, "E556.filletArc", {"start": v(5.58, 54.52) * mm, "mid": v(6.32, 52.72) * mm, "end": v(8.12, 51.98) * mm});
            skPoint(sketch, "E557.visualSharp", {"position": v(28.25, 49.44) * mm});
            skArc(sketch, "E557.filletArc", {"start": v(28.25, 46.9) * mm, "mid": v(27.5, 48.7) * mm, "end": v(25.7, 49.44) * mm});
            skPoint(sketch, "E558.visualSharp", {"position": v(30.79, 49.44) * mm});
            skArc(sketch, "E558.filletArc", {"start": v(33.33, 49.44) * mm, "mid": v(31.53, 48.7) * mm, "end": v(30.79, 46.9) * mm});
            skPoint(sketch, "E559.visualSharp", {"position": v(3.04, 51.98) * mm});
            skArc(sketch, "E559.filletArc", {"start": v(0.5, 51.98) * mm, "mid": v(2.3, 52.72) * mm, "end": v(3.04, 54.52) * mm});
            skArc(sketch, "E560", {"start": v(20.46, 49.44) * mm, "mid": v(18.9, 48.8) * mm, "end": v(18.24, 47.24) * mm});
            skArc(sketch, "E561", {"start": v(18.24, 53.71) * mm, "mid": v(18.7, 52.52) * mm, "end": v(19.87, 51.98) * mm});
            skArc(sketch, "E562", {"start": v(13.42, 51.98) * mm, "mid": v(15.03, 52.65) * mm, "end": v(15.7, 54.26) * mm});
            skArc(sketch, "E563", {"start": v(15.7, 47.91) * mm, "mid": v(15.21, 49.03) * mm, "end": v(14.07, 49.44) * mm});
            skLineSegment(sketch, "E564.0", {"start": v(-9.67, -16.62) * mm, "end": v(-9.67, -23.12) * mm});
            skArc(sketch, "E565", {"start": v(-7.12, -24.06) * mm, "mid": v(-6.6, -25.02) * mm, "end": v(-5.59, -25.41) * mm});
            skArc(sketch, "E566", {"start": v(-12.12, -25.41) * mm, "mid": v(-10.37, -24.74) * mm, "end": v(-9.67, -23.01) * mm});
            skArc(sketch, "E567", {"start": v(-75.33, -38.11) * mm, "mid": v(-73.9, -37.55) * mm, "end": v(-73.16, -36.22) * mm});
            skArc(sketch, "E568", {"start": v(19.6, -2.55) * mm, "mid": v(18.48, -3.16) * mm, "end": v(18.08, -4.38) * mm});
            skArc(sketch, "E569", {"start": v(26.7, -12.71) * mm, "mid": v(27.94, -12.02) * mm, "end": v(28.43, -10.7) * mm});
            skArc(sketch, "E570", {"start": v(73.84, 42.41) * mm, "mid": v(75.65, 43.55) * mm, "end": v(74.51, 45.36) * mm});
            skArc(sketch, "E571", {"start": v(51.24, 50.64) * mm, "mid": v(49.38, 49.32) * mm, "end": v(50.9, 47.63) * mm});
            skLineSegment(sketch, "E572", {"start": v(51.24, 50.64) * mm, "end": v(74.51, 45.36) * mm});
            skLineSegment(sketch, "E573", {"start": v(50.9, 47.63) * mm, "end": v(73.84, 42.41) * mm});
            skArc(sketch, "E574", {"start": v(-14.64, 65.44) * mm, "mid": v(-16.53, 64.28) * mm, "end": v(-15.32, 62.42) * mm});
            skArc(sketch, "E575", {"start": v(7.92, 57.68) * mm, "mid": v(9.88, 58.82) * mm, "end": v(8.66, 60.72) * mm});
            skLineSegment(sketch, "E576", {"start": v(-14.77, 65.47) * mm, "end": v(8.66, 60.72) * mm});
            skLineSegment(sketch, "E577", {"start": v(8.16, 57.63) * mm, "end": v(-15.32, 62.42) * mm});
            skArc(sketch, "E578", {"start": v(17.2, 58.97) * mm, "mid": v(15.5, 57.69) * mm, "end": v(16.7, 55.92) * mm});
            skArc(sketch, "E579", {"start": v(40.03, 50.4) * mm, "mid": v(41.9, 51.55) * mm, "end": v(40.74, 53.41) * mm});
            skLineSegment(sketch, "E580", {"start": v(17.2, 58.97) * mm, "end": v(40.74, 53.41) * mm});
            skLineSegment(sketch, "E581", {"start": v(16.7, 55.92) * mm, "end": v(40.03, 50.4) * mm});
            skArc(sketch, "E582", {"start": v(48.65, -65.1) * mm, "mid": v(50.69, -64.13) * mm, "end": v(49.62, -62.15) * mm});
            skArc(sketch, "E583", {"start": v(26.94, -54.9) * mm, "mid": v(24.92, -55.9) * mm, "end": v(26.06, -57.84) * mm});
            skArc(sketch, "E584", {"start": v(49.62, -62.15) * mm, "mid": v(38.2, -58.4) * mm, "end": v(26.71, -54.84) * mm});
            skArc(sketch, "E585", {"start": v(48.75, -65.13) * mm, "mid": v(37.44, -61.36) * mm, "end": v(26.06, -57.84) * mm});
            skArc(sketch, "E586", {"start": v(13, -55.52) * mm, "mid": v(14.94, -54.21) * mm, "end": v(13.41, -52.45) * mm});
            skLineSegment(sketch, "E587", {"start": v(14.97, -54.13) * mm, "end": v(14.95, -54.13) * mm});
            skArc(sketch, "E588", {"start": v(-10.47, -51.04) * mm, "mid": v(-12.07, -52.6) * mm, "end": v(-10.45, -54.15) * mm});
            skArc(sketch, "E589", {"start": v(13.34, -55.57) * mm, "mid": v(1.44, -54.39) * mm, "end": v(-10.51, -54.15) * mm});
            skArc(sketch, "E590", {"start": v(13.41, -52.45) * mm, "mid": v(1.5, -51.28) * mm, "end": v(-10.47, -51.04) * mm});
            skArc(sketch, "E591", {"start": v(-24, -55.22) * mm, "mid": v(-22.72, -53.43) * mm, "end": v(-24.52, -52.17) * mm});
            skArc(sketch, "E592", {"start": v(-48.3, -56.48) * mm, "mid": v(-49.7, -58.22) * mm, "end": v(-47.89, -59.54) * mm});
            skLineSegment(sketch, "E593", {"start": v(-48.58, -56.53) * mm, "end": v(-24.52, -52.17) * mm});
            skLineSegment(sketch, "E594", {"start": v(-24, -55.22) * mm, "end": v(-47.89, -59.54) * mm});
            skPoint(sketch, "E595.start.orphan", {"position": v(-22.7, -53.64) * mm});
            skLineSegment(sketch, "E596", {"start": v(28.43, 15.23) * mm, "end": v(28.43, 7.6) * mm});
            skLineSegment(sketch, "E597", {"start": v(84.04, 24.04) * mm, "end": v(80.9, 24.04) * mm});
            skLineSegment(sketch, "E598.trimOffspring", {"start": v(-70.62, 24.04) * mm, "end": v(-60.46, 24.04) * mm});
            skLineSegment(sketch, "E599.trimOffspring", {"start": v(-57.92, 24.04) * mm, "end": v(-47.76, 24.04) * mm});
            skLineSegment(sketch, "E600.trimOffspring", {"start": v(-4.58, 24.04) * mm, "end": v(3.04, 24.04) * mm});
            skLineSegment(sketch, "E601.trimOffspring", {"start": v(5.58, 24.04) * mm, "end": v(13.16, 24.04) * mm});
            skLineSegment(sketch, "E602", {"start": v(-68.08, -27.95) * mm, "end": v(-63, -27.95) * mm});
            skLineSegment(sketch, "E603", {"start": v(-70.62, -30.5) * mm, "end": v(-70.6, -38.16) * mm});
            skLineSegment(sketch, "E604", {"start": v(-60.46, -30.5) * mm, "end": v(-60.5, -37.49) * mm});
            skSolve(sketch);
        }
        {
            var Q0;
            Q0=makeQuery(id+"F7.imprint","IMPRINT",FACE,{"disambiguationData":[TD([[makeQuery(id+"F7.imprint","IMPRINT",EDGE,{"derivedFrom":sQuery(id+"F7.wireOp",EDGE,"E7")}),-1.0]])]});
            var Q1;
            Q1=makeQuery(id+"F7.imprint","IMPRINT",FACE,{"disambiguationData":[TD([[makeQuery(id+"F7.imprint","IMPRINT",EDGE,{"derivedFrom":sQuery(id+"F7.wireOp",EDGE,"E33")}),-1.0]])]});
            var Q2;
            Q2=makeQuery(id+"F7.imprint","IMPRINT",FACE,{"disambiguationData":[TD([[makeQuery(id+"F7.imprint","IMPRINT",EDGE,{"derivedFrom":sQuery(id+"F7.wireOp",EDGE,"E60")}),-1.0]])]});
            var Q3;
            Q3=makeQuery(id+"F7.imprint","IMPRINT",FACE,{"disambiguationData":[TD([[makeQuery(id+"F7.imprint","IMPRINT",EDGE,{"derivedFrom":sQuery(id+"F7.wireOp",EDGE,"E39")}),-1.0]])]});
            var Q4;
            {var subQ11=sQuery(id+"F7.wireOp",EDGE,"E30.filletArc");Q4=makeQuery(id+"F7.imprint","IMPRINT",FACE,{"disambiguationData":[TD([[makeQuery(id+"F7.imprint","IMPRINT",EDGE,{"derivedFrom":subQ11}),1.0]])]});}
            extrude(context, id + "F0", {"entities" : qUnion([Q0, Q1, Q2, Q3, Q4]), "depth" : 3.17 * mm});
        }
        {
            var Q0;
            Q0=makeQuery(id+"F7.imprint","IMPRINT",FACE,{"disambiguationData":[TD([[makeQuery(id+"F7.imprint","IMPRINT",EDGE,{"derivedFrom":sQuery(id+"F7.wireOp",EDGE,"E70.0")}),-1.0]])]});
            var Q1;
            Q1=makeQuery(id+"F7.imprint","IMPRINT",FACE,{"disambiguationData":[TD([[makeQuery(id+"F7.imprint","IMPRINT",EDGE,{"derivedFrom":sQuery(id+"F7.wireOp",EDGE,"E39")}),1.0]])]});
            extrude(context, id + "F1", {"entities" : qUnion([Q0, Q1]), "depth" : 1.52 * mm});
        }
        {
            var Q0;
            Q0=makeQuery(id+"F7.imprint","IMPRINT",FACE,{"disambiguationData":[TD([[makeQuery(id+"F7.imprint","IMPRINT",EDGE,{"derivedFrom":sQuery(id+"F7.wireOp",EDGE,"E43.0")}),1.0]])]});
            var Q1;
            Q1=makeQuery(id+"F7.imprint","IMPRINT",FACE,{"disambiguationData":[TD([[makeQuery(id+"F7.imprint","IMPRINT",EDGE,{"derivedFrom":sQuery(id+"F7.wireOp",EDGE,"E79")}),1.0]])]});
            var Q2;
            Q2=makeQuery(id+"F7.imprint","IMPRINT",FACE,{"disambiguationData":[TD([[makeQuery(id+"F7.imprint","IMPRINT",EDGE,{"derivedFrom":sQuery(id+"F7.wireOp",EDGE,"E82")}),-1.0]])]});
            extrude(context, id + "F2", {"entities" : qUnion([Q0, Q1, Q2]), "depth" : 5.08 * mm});
        }
        {
            var Q0;
            {var subQ104=sQuery(id+"F7.wireOp",EDGE,"E91.0");Q0=makeQuery(id+"F7.imprint","IMPRINT",FACE,{"disambiguationData":[TD([[makeQuery(id+"F7.imprint","IMPRINT",EDGE,{"derivedFrom":subQ104}),-1.0]])]});}
            var Q1;
            {var subQ0=sQuery(id+"F7.wireOp",EDGE,"E129.trimOffspring");Q1=makeQuery(id+"F7.imprint","IMPRINT",FACE,{"disambiguationData":[TD([[makeQuery(id+"F7.imprint","IMPRINT",EDGE,{"derivedFrom":subQ0}),-1.0]])]});}
            var Q2;
            {var subQ0=sQuery(id+"F7.wireOp",EDGE,"E130.trimOffspring");Q2=makeQuery(id+"F7.imprint","IMPRINT",FACE,{"disambiguationData":[TD([[makeQuery(id+"F7.imprint","IMPRINT",EDGE,{"derivedFrom":subQ0}),-1.0]])]});}
            var Q3;
            {var subQ0=sQuery(id+"F7.wireOp",EDGE,"E131.trimOffspring");Q3=makeQuery(id+"F7.imprint","IMPRINT",FACE,{"disambiguationData":[TD([[makeQuery(id+"F7.imprint","IMPRINT",EDGE,{"derivedFrom":subQ0}),-1.0]])]});}
            var Q4;
            {var subQ0=sQuery(id+"F7.wireOp",EDGE,"E132.trimOffspring");Q4=makeQuery(id+"F7.imprint","IMPRINT",FACE,{"disambiguationData":[TD([[makeQuery(id+"F7.imprint","IMPRINT",EDGE,{"derivedFrom":subQ0}),-1.0]])]});}
            var Q5;
            {var subQ0=sQuery(id+"F7.wireOp",EDGE,"E292.trimOffspring");Q5=makeQuery(id+"F7.imprint","IMPRINT",FACE,{"disambiguationData":[TD([[makeQuery(id+"F7.imprint","IMPRINT",EDGE,{"derivedFrom":subQ0}),-1.0]])]});}
            var Q6;
            {var subQ0=sQuery(id+"F7.wireOp",EDGE,"E290.trimOffspring");Q6=makeQuery(id+"F7.imprint","IMPRINT",FACE,{"disambiguationData":[TD([[makeQuery(id+"F7.imprint","IMPRINT",EDGE,{"derivedFrom":subQ0}),-1.0]])]});}
            var Q7;
            {var subQ0=sQuery(id+"F7.wireOp",EDGE,"E135.trimOffspring");Q7=makeQuery(id+"F7.imprint","IMPRINT",FACE,{"disambiguationData":[TD([[makeQuery(id+"F7.imprint","IMPRINT",EDGE,{"derivedFrom":subQ0}),-1.0]])]});}
            var Q8;
            {var subQ0=sQuery(id+"F7.wireOp",EDGE,"E136.trimOffspring");Q8=makeQuery(id+"F7.imprint","IMPRINT",FACE,{"disambiguationData":[TD([[makeQuery(id+"F7.imprint","IMPRINT",EDGE,{"derivedFrom":subQ0}),-1.0]])]});}
            var Q9;
            {var subQ0=sQuery(id+"F7.wireOp",EDGE,"E133.trimOffspring");Q9=makeQuery(id+"F7.imprint","IMPRINT",FACE,{"disambiguationData":[TD([[makeQuery(id+"F7.imprint","IMPRINT",EDGE,{"derivedFrom":subQ0}),-1.0]])]});}
            var Q10;
            {var subQ0=sQuery(id+"F7.wireOp",EDGE,"E134.trimOffspring");Q10=makeQuery(id+"F7.imprint","IMPRINT",FACE,{"disambiguationData":[TD([[makeQuery(id+"F7.imprint","IMPRINT",EDGE,{"derivedFrom":subQ0}),-1.0]])]});}
            var Q11;
            {var subQ14=sQuery(id+"F7.wireOp",EDGE,"E96.trimOffspring");Q11=makeQuery(id+"F7.imprint","IMPRINT",FACE,{"disambiguationData":[TD([[makeQuery(id+"F7.imprint","IMPRINT",EDGE,{"derivedFrom":subQ14}),-1.0]])]});}
            var Q12;
            {var subQ8=sQuery(id+"F7.wireOp",EDGE,"E56.filletArc");Q12=makeQuery(id+"F7.imprint","IMPRINT",FACE,{"disambiguationData":[TD([[makeQuery(id+"F7.imprint","IMPRINT",EDGE,{"derivedFrom":subQ8}),1.0]])]});}
            var Q13;
            {var subQ0=sQuery(id+"F7.wireOp",EDGE,"E112.0");Q13=makeQuery(id+"F7.imprint","IMPRINT",FACE,{"disambiguationData":[TD([[makeQuery(id+"F7.imprint","IMPRINT",EDGE,{"derivedFrom":subQ0}),-1.0]])]});}
            var Q14;
            {var subQ0=sQuery(id+"F7.wireOp",EDGE,"E126.trimOffspring");Q14=makeQuery(id+"F7.imprint","IMPRINT",FACE,{"disambiguationData":[TD([[makeQuery(id+"F7.imprint","IMPRINT",EDGE,{"derivedFrom":subQ0}),-1.0]])]});}
            var Q15;
            {var subQ0=sQuery(id+"F7.wireOp",EDGE,"E127.trimOffspring");Q15=makeQuery(id+"F7.imprint","IMPRINT",FACE,{"disambiguationData":[TD([[makeQuery(id+"F7.imprint","IMPRINT",EDGE,{"derivedFrom":subQ0}),-1.0]])]});}
            extrude(context, id + "F3", {"entities" : qUnion([Q0, Q1, Q2, Q3, Q4, Q5, Q6, Q7, Q8, Q9, Q10, Q11, Q12, Q13, Q14, Q15]), "depth" : 1.52 * mm});
        }
        {
            var Q0;
            Q0=makeQuery(id+"F0.opExtrude","CAP_FACE",FACE,{"disambiguationData":[OSD([sQuery(id+"F7.wireOp",EDGE,"E7"),sQuery(id+"F7.wireOp",EDGE,"E8"),sQuery(id+"F7.wireOp",EDGE,"E9"),sQuery(id+"F7.wireOp",EDGE,"E10"),sQuery(id+"F7.wireOp",EDGE,"E11"),sQuery(id+"F7.wireOp",EDGE,"E12.filletArc"),sQuery(id+"F7.wireOp",EDGE,"E13.filletArc"),sQuery(id+"F7.wireOp",EDGE,"E14.filletArc"),sQuery(id+"F7.wireOp",EDGE,"E15.filletArc"),sQuery(id+"F7.wireOp",EDGE,"E51.0"),sQuery(id+"F7.wireOp",EDGE,"E52.0"),sQuery(id+"F7.wireOp",EDGE,"E53.0"),sQuery(id+"F7.wireOp",EDGE,"E54.0"),sQuery(id+"F7.wireOp",EDGE,"E55.0"),sQuery(id+"F7.wireOp",EDGE,"E56.filletArc"),sQuery(id+"F7.wireOp",EDGE,"E58.filletArc"),sQuery(id+"F7.wireOp",EDGE,"E59.filletArc"),sQuery(id+"F7.wireOp",EDGE,"E110"),sQuery(id+"F7.wireOp",EDGE,"E546.trimOffspring"),sQuery(id+"F7.wireOp",EDGE,"E570"),sQuery(id+"F7.wireOp",EDGE,"E571"),sQuery(id+"F7.wireOp",EDGE,"E572"),sQuery(id+"F7.wireOp",EDGE,"E573"),sQuery(id+"F7.wireOp",EDGE,"E574"),sQuery(id+"F7.wireOp",EDGE,"E575"),sQuery(id+"F7.wireOp",EDGE,"E576"),sQuery(id+"F7.wireOp",EDGE,"E577"),sQuery(id+"F7.wireOp",EDGE,"E578"),sQuery(id+"F7.wireOp",EDGE,"E579"),sQuery(id+"F7.wireOp",EDGE,"E580"),sQuery(id+"F7.wireOp",EDGE,"E581"),sQuery(id+"F7.wireOp",EDGE,"E582"),sQuery(id+"F7.wireOp",EDGE,"E583"),sQuery(id+"F7.wireOp",EDGE,"E584"),sQuery(id+"F7.wireOp",EDGE,"E585"),sQuery(id+"F7.wireOp",EDGE,"E586"),sQuery(id+"F7.wireOp",EDGE,"E588"),sQuery(id+"F7.wireOp",EDGE,"E589"),sQuery(id+"F7.wireOp",EDGE,"E590"),sQuery(id+"F7.wireOp",EDGE,"E591"),sQuery(id+"F7.wireOp",EDGE,"E592"),sQuery(id+"F7.wireOp",EDGE,"E593"),sQuery(id+"F7.wireOp",EDGE,"E594")])],"isStart":false});
            chamfer(context, id + "F4", {"entities" : qUnion([Q0]), "width" : 0.38 * mm, "tangentPropagation" : true});
        }
        {
            var Q0;
            Q0=makeQuery(id+"F0.opExtrude","CAP_EDGE",EDGE,{"disambiguationData":[OSD([sQuery(id+"F7.wireOp",EDGE,"E10")])],"isStart":true});
            var Q1;
            Q1=makeQuery(id+"F0.opExtrude","CAP_EDGE",EDGE,{"disambiguationData":[OSD([sQuery(id+"F7.wireOp",EDGE,"E594")])],"isStart":true});
            var Q2;
            Q2=makeQuery(id+"F0.opExtrude","CAP_EDGE",EDGE,{"disambiguationData":[OSD([sQuery(id+"F7.wireOp",EDGE,"E592")])],"isStart":true});
            var Q3;
            Q3=makeQuery(id+"F0.opExtrude","CAP_EDGE",EDGE,{"disambiguationData":[OSD([sQuery(id+"F7.wireOp",EDGE,"E593")])],"isStart":true});
            var Q4;
            Q4=makeQuery(id+"F0.opExtrude","CAP_EDGE",EDGE,{"disambiguationData":[OSD([sQuery(id+"F7.wireOp",EDGE,"E589")])],"isStart":true});
            var Q5;
            Q5=makeQuery(id+"F0.opExtrude","CAP_EDGE",EDGE,{"disambiguationData":[OSD([sQuery(id+"F7.wireOp",EDGE,"E588")])],"isStart":true});
            var Q6;
            Q6=makeQuery(id+"F0.opExtrude","CAP_EDGE",EDGE,{"disambiguationData":[OSD([sQuery(id+"F7.wireOp",EDGE,"E590")])],"isStart":true});
            var Q7;
            Q7=makeQuery(id+"F0.opExtrude","CAP_EDGE",EDGE,{"disambiguationData":[OSD([sQuery(id+"F7.wireOp",EDGE,"E586")])],"isStart":true});
            var Q8;
            Q8=makeQuery(id+"F0.opExtrude","CAP_EDGE",EDGE,{"disambiguationData":[OSD([sQuery(id+"F7.wireOp",EDGE,"E585")])],"isStart":true});
            var Q9;
            Q9=makeQuery(id+"F0.opExtrude","CAP_EDGE",EDGE,{"disambiguationData":[OSD([sQuery(id+"F7.wireOp",EDGE,"E583")])],"isStart":true});
            var Q10;
            Q10=makeQuery(id+"F0.opExtrude","CAP_EDGE",EDGE,{"disambiguationData":[OSD([sQuery(id+"F7.wireOp",EDGE,"E584")])],"isStart":true});
            var Q11;
            Q11=makeQuery(id+"F0.opExtrude","CAP_EDGE",EDGE,{"disambiguationData":[OSD([sQuery(id+"F7.wireOp",EDGE,"E582")])],"isStart":true});
            var Q12;
            Q12=makeQuery(id+"F0.opExtrude","CAP_EDGE",EDGE,{"disambiguationData":[OSD([sQuery(id+"F7.wireOp",EDGE,"E36")])],"isStart":true});
            var Q13;
            Q13=makeQuery(id+"F0.opExtrude","CAP_EDGE",EDGE,{"disambiguationData":[OSD([sQuery(id+"F7.wireOp",EDGE,"E33")])],"isStart":true});
            var Q14;
            Q14=makeQuery(id+"F0.opExtrude","CAP_EDGE",EDGE,{"disambiguationData":[OSD([sQuery(id+"F7.wireOp",EDGE,"E34")])],"isStart":true});
            var Q15;
            Q15=makeQuery(id+"F0.opExtrude","CAP_EDGE",EDGE,{"disambiguationData":[OSD([sQuery(id+"F7.wireOp",EDGE,"E35")])],"isStart":true});
            var Q16;
            Q16=makeQuery(id+"F0.opExtrude","CAP_EDGE",EDGE,{"disambiguationData":[OSD([sQuery(id+"F7.wireOp",EDGE,"E63")])],"isStart":true});
            var Q17;
            Q17=makeQuery(id+"F0.opExtrude","CAP_EDGE",EDGE,{"disambiguationData":[OSD([sQuery(id+"F7.wireOp",EDGE,"E60")])],"isStart":true});
            var Q18;
            Q18=makeQuery(id+"F0.opExtrude","CAP_EDGE",EDGE,{"disambiguationData":[OSD([sQuery(id+"F7.wireOp",EDGE,"E62")])],"isStart":true});
            var Q19;
            Q19=makeQuery(id+"F0.opExtrude","CAP_EDGE",EDGE,{"disambiguationData":[OSD([sQuery(id+"F7.wireOp",EDGE,"E61")])],"isStart":true});
            fillet(context, id + "F5", {"entities" : qUnion([Q0, Q1, Q2, Q3, Q4, Q5, Q6, Q7, Q8, Q9, Q10, Q11, Q12, Q13, Q14, Q15, Q16, Q17, Q18, Q19]), "radius" : 0.38 * mm, "tangentPropagation" : true, "allowEdgeOverflow" : false});
        }
        {
            var Q0;
            Q0=makeQuery(id+"F0.opExtrude","CAP_EDGE",EDGE,{"disambiguationData":[OSD([sQuery(id+"F7.wireOp",EDGE,"E35")])],"isStart":false});
            var Q1;
            Q1=makeQuery(id+"F0.opExtrude","CAP_EDGE",EDGE,{"disambiguationData":[OSD([sQuery(id+"F7.wireOp",EDGE,"E33")])],"isStart":false});
            var Q2;
            Q2=makeQuery(id+"F0.opExtrude","CAP_EDGE",EDGE,{"disambiguationData":[OSD([sQuery(id+"F7.wireOp",EDGE,"E36")])],"isStart":false});
            var Q3;
            Q3=makeQuery(id+"F0.opExtrude","CAP_EDGE",EDGE,{"disambiguationData":[OSD([sQuery(id+"F7.wireOp",EDGE,"E34")])],"isStart":false});
            var Q4;
            Q4=makeQuery(id+"F0.opExtrude","CAP_EDGE",EDGE,{"disambiguationData":[OSD([sQuery(id+"F7.wireOp",EDGE,"E62")])],"isStart":false});
            var Q5;
            Q5=makeQuery(id+"F0.opExtrude","CAP_EDGE",EDGE,{"disambiguationData":[OSD([sQuery(id+"F7.wireOp",EDGE,"E60")])],"isStart":false});
            var Q6;
            Q6=makeQuery(id+"F0.opExtrude","CAP_EDGE",EDGE,{"disambiguationData":[OSD([sQuery(id+"F7.wireOp",EDGE,"E63")])],"isStart":false});
            var Q7;
            Q7=makeQuery(id+"F0.opExtrude","CAP_EDGE",EDGE,{"disambiguationData":[OSD([sQuery(id+"F7.wireOp",EDGE,"E61")])],"isStart":false});
            fillet(context, id + "F6", {"entities" : qUnion([Q0, Q1, Q2, Q3, Q4, Q5, Q6, Q7]), "radius" : 0.38 * mm, "tangentPropagation" : true, "allowEdgeOverflow" : false});
        }
    });
